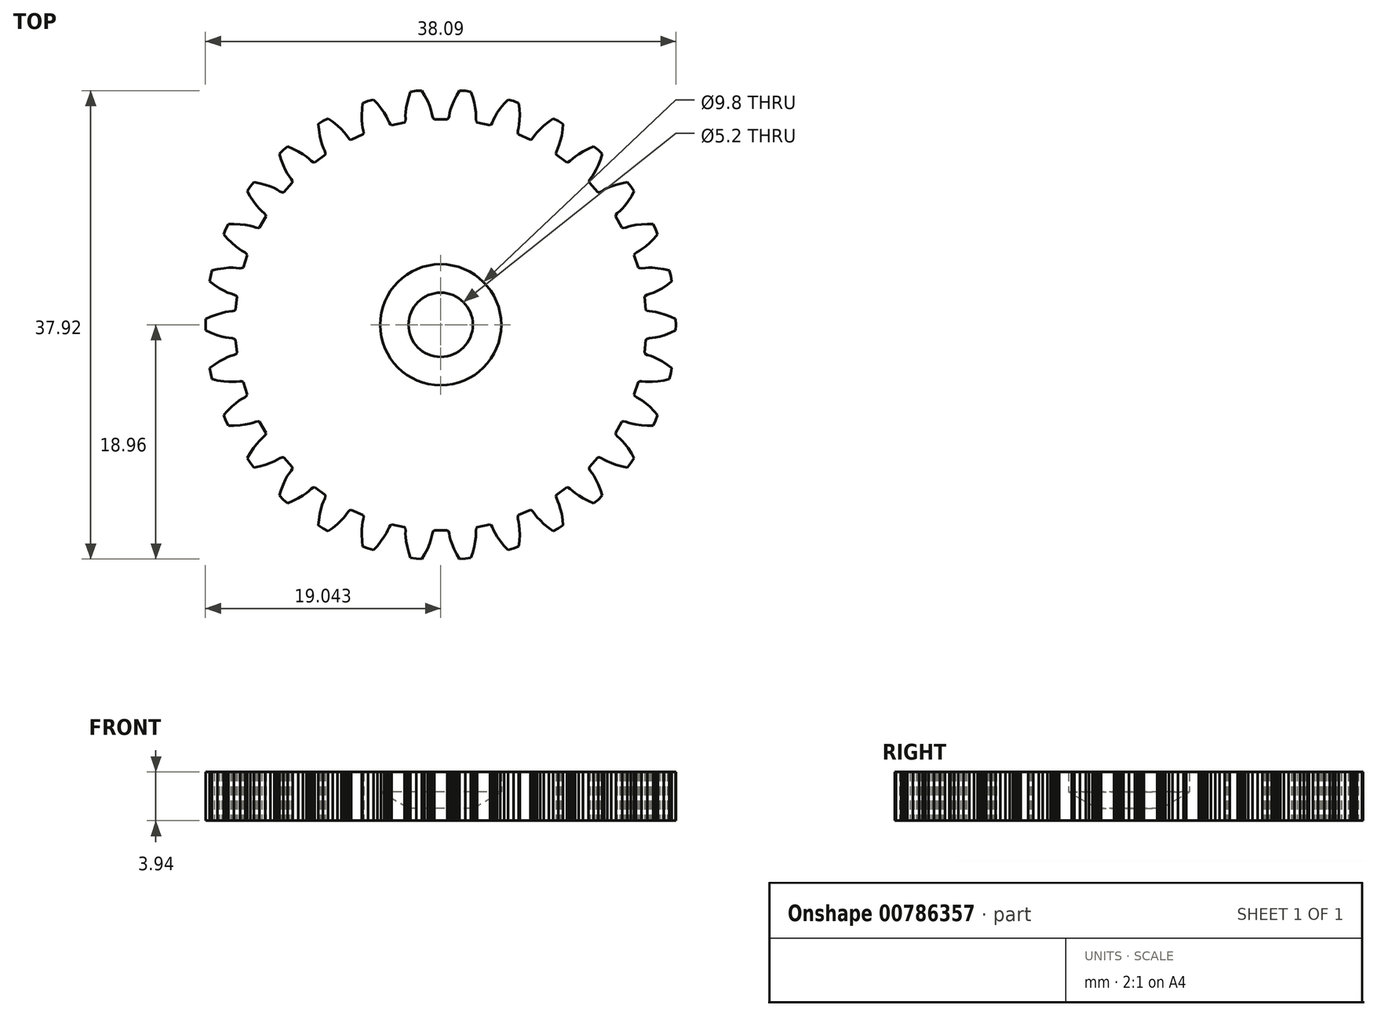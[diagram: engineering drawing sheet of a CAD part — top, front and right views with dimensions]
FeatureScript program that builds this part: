
annotation { "Feature Type Name" : "Feature", "Feature Type Description" : "" }
export const myFeature = defineFeature(function(context is Context, id is Id, definition is map)
    precondition{}
    {
        {
            var Q0;
            Q0=qCreatedBy(makeId("Top.planeOp"),FACE);
            var sketch = newSketch(context, id + "F0", { "sketchPlane" : qUnion([Q0])});
            skLineSegment(sketch, "E0", {"start": v(756.52, -239.33) * mm, "end": v(762.99, -215.17) * mm});
            skLineSegment(sketch, "E1", {"start": v(762.99, -215.17) * mm, "end": v(766.9, -190.46) * mm});
            skLineSegment(sketch, "E2", {"start": v(766.9, -190.46) * mm, "end": v(747.41, -175.84) * mm});
            skLineSegment(sketch, "E3", {"start": v(747.41, -175.84) * mm, "end": v(724.34, -160.92) * mm});
            skLineSegment(sketch, "E4", {"start": v(724.34, -160.92) * mm, "end": v(704.2, -149.81) * mm});
            skLineSegment(sketch, "E5", {"start": v(704.2, -149.81) * mm, "end": v(687.39, -142.02) * mm});
            skLineSegment(sketch, "E6", {"start": v(687.39, -142.02) * mm, "end": v(674.26, -137) * mm});
            skLineSegment(sketch, "E7", {"start": v(674.26, -137) * mm, "end": v(660.16, -132.73) * mm});
            skLineSegment(sketch, "E8", {"start": v(660.16, -132.73) * mm, "end": v(651.05, -128.15) * mm});
            skLineSegment(sketch, "E9", {"start": v(651.05, -128.15) * mm, "end": v(647, -123.28) * mm});
            skLineSegment(sketch, "E10", {"start": v(647, -123.28) * mm, "end": v(653.04, -65.76) * mm});
            skLineSegment(sketch, "E11", {"start": v(653.04, -65.76) * mm, "end": v(658.02, -61.84) * mm});
            skLineSegment(sketch, "E12", {"start": v(658.02, -61.84) * mm, "end": v(667.88, -59.26) * mm});
            skLineSegment(sketch, "E13", {"start": v(667.88, -59.26) * mm, "end": v(682.56, -58) * mm});
            skLineSegment(sketch, "E14", {"start": v(682.56, -58) * mm, "end": v(696.45, -55.83) * mm});
            skLineSegment(sketch, "E15", {"start": v(696.45, -55.83) * mm, "end": v(714.5, -51.7) * mm});
            skLineSegment(sketch, "E16", {"start": v(714.5, -51.7) * mm, "end": v(736.52, -45.02) * mm});
            skLineSegment(sketch, "E17", {"start": v(736.52, -45.02) * mm, "end": v(762.2, -35.23) * mm});
            skLineSegment(sketch, "E18", {"start": v(762.2, -35.23) * mm, "end": v(784.3, -24.98) * mm});
            skLineSegment(sketch, "E19", {"start": v(784.3, -24.98) * mm, "end": v(785.6, 0) * mm});
            skLineSegment(sketch, "E20", {"start": v(785.6, 0) * mm, "end": v(784.3, 24.98) * mm});
            skLineSegment(sketch, "E21", {"start": v(784.3, 24.98) * mm, "end": v(762.2, 35.23) * mm});
            skLineSegment(sketch, "E22", {"start": v(762.2, 35.23) * mm, "end": v(736.52, 45.02) * mm});
            skLineSegment(sketch, "E23", {"start": v(736.52, 45.02) * mm, "end": v(714.5, 51.7) * mm});
            skLineSegment(sketch, "E24", {"start": v(714.5, 51.7) * mm, "end": v(696.45, 55.83) * mm});
            skLineSegment(sketch, "E25", {"start": v(696.45, 55.83) * mm, "end": v(682.56, 58) * mm});
            skLineSegment(sketch, "E26", {"start": v(682.56, 58) * mm, "end": v(667.88, 59.26) * mm});
            skLineSegment(sketch, "E27", {"start": v(667.88, 59.26) * mm, "end": v(658.02, 61.84) * mm});
            skLineSegment(sketch, "E28", {"start": v(658.02, 61.84) * mm, "end": v(653.04, 65.76) * mm});
            skLineSegment(sketch, "E29", {"start": v(653.04, 65.76) * mm, "end": v(647, 123.28) * mm});
            skLineSegment(sketch, "E30", {"start": v(647, 123.28) * mm, "end": v(651.05, 128.15) * mm});
            skLineSegment(sketch, "E31", {"start": v(651.05, 128.15) * mm, "end": v(660.16, 132.73) * mm});
            skLineSegment(sketch, "E32", {"start": v(660.16, 132.73) * mm, "end": v(674.26, 137) * mm});
            skLineSegment(sketch, "E33", {"start": v(674.26, 137) * mm, "end": v(687.39, 142.02) * mm});
            skLineSegment(sketch, "E34", {"start": v(687.39, 142.02) * mm, "end": v(704.2, 149.81) * mm});
            skLineSegment(sketch, "E35", {"start": v(704.2, 149.81) * mm, "end": v(724.34, 160.92) * mm});
            skLineSegment(sketch, "E36", {"start": v(724.34, 160.92) * mm, "end": v(747.41, 175.84) * mm});
            skLineSegment(sketch, "E37", {"start": v(747.41, 175.84) * mm, "end": v(766.9, 190.46) * mm});
            skLineSegment(sketch, "E38", {"start": v(766.9, 190.46) * mm, "end": v(762.99, 215.17) * mm});
            skLineSegment(sketch, "E39", {"start": v(762.99, 215.17) * mm, "end": v(756.52, 239.33) * mm});
            skLineSegment(sketch, "E40", {"start": v(756.52, 239.33) * mm, "end": v(732.77, 244.76) * mm});
            skLineSegment(sketch, "E41", {"start": v(732.77, 244.76) * mm, "end": v(705.62, 249) * mm});
            skLineSegment(sketch, "E42", {"start": v(705.62, 249) * mm, "end": v(682.7, 250.96) * mm});
            skLineSegment(sketch, "E43", {"start": v(682.7, 250.96) * mm, "end": v(664.17, 251.24) * mm});
            skLineSegment(sketch, "E44", {"start": v(664.17, 251.24) * mm, "end": v(650.14, 250.48) * mm});
            skLineSegment(sketch, "E45", {"start": v(650.14, 250.48) * mm, "end": v(635.52, 248.65) * mm});
            skLineSegment(sketch, "E46", {"start": v(635.52, 248.65) * mm, "end": v(625.33, 249.13) * mm});
            skLineSegment(sketch, "E47", {"start": v(625.33, 249.13) * mm, "end": v(619.65, 251.93) * mm});
            skLineSegment(sketch, "E48", {"start": v(619.65, 251.93) * mm, "end": v(601.78, 306.93) * mm});
            skLineSegment(sketch, "E49", {"start": v(601.78, 306.93) * mm, "end": v(604.73, 312.54) * mm});
            skLineSegment(sketch, "E50", {"start": v(604.73, 312.54) * mm, "end": v(612.69, 318.91) * mm});
            skLineSegment(sketch, "E51", {"start": v(612.69, 318.91) * mm, "end": v(625.6, 326.03) * mm});
            skLineSegment(sketch, "E52", {"start": v(625.6, 326.03) * mm, "end": v(637.4, 333.66) * mm});
            skLineSegment(sketch, "E53", {"start": v(637.4, 333.66) * mm, "end": v(652.21, 344.78) * mm});
            skLineSegment(sketch, "E54", {"start": v(652.21, 344.78) * mm, "end": v(669.6, 359.83) * mm});
            skLineSegment(sketch, "E55", {"start": v(669.6, 359.83) * mm, "end": v(689.07, 379.22) * mm});
            skLineSegment(sketch, "E56", {"start": v(689.07, 379.22) * mm, "end": v(705.1, 397.58) * mm});
            skLineSegment(sketch, "E57", {"start": v(705.1, 397.58) * mm, "end": v(696.13, 420.93) * mm});
            skLineSegment(sketch, "E58", {"start": v(696.13, 420.93) * mm, "end": v(684.78, 443.21) * mm});
            skLineSegment(sketch, "E59", {"start": v(684.78, 443.21) * mm, "end": v(660.42, 443.59) * mm});
            skLineSegment(sketch, "E60", {"start": v(660.42, 443.59) * mm, "end": v(632.98, 442.1) * mm});
            skLineSegment(sketch, "E61", {"start": v(632.98, 442.1) * mm, "end": v(610.15, 439.24) * mm});
            skLineSegment(sketch, "E62", {"start": v(610.15, 439.24) * mm, "end": v(591.97, 435.67) * mm});
            skLineSegment(sketch, "E63", {"start": v(591.97, 435.67) * mm, "end": v(578.41, 432) * mm});
            skLineSegment(sketch, "E64", {"start": v(578.41, 432) * mm, "end": v(564.49, 427.18) * mm});
            skLineSegment(sketch, "E65", {"start": v(564.49, 427.18) * mm, "end": v(554.43, 425.53) * mm});
            skLineSegment(sketch, "E66", {"start": v(554.43, 425.53) * mm, "end": v(548.28, 427.08) * mm});
            skLineSegment(sketch, "E67", {"start": v(548.28, 427.08) * mm, "end": v(519.37, 477.17) * mm});
            skLineSegment(sketch, "E68", {"start": v(519.37, 477.17) * mm, "end": v(521.09, 483.27) * mm});
            skLineSegment(sketch, "E69", {"start": v(521.09, 483.27) * mm, "end": v(527.55, 491.16) * mm});
            skLineSegment(sketch, "E70", {"start": v(527.55, 491.16) * mm, "end": v(538.7, 500.8) * mm});
            skLineSegment(sketch, "E71", {"start": v(538.7, 500.8) * mm, "end": v(548.65, 510.72) * mm});
            skLineSegment(sketch, "E72", {"start": v(548.65, 510.72) * mm, "end": v(560.83, 524.67) * mm});
            skLineSegment(sketch, "E73", {"start": v(560.83, 524.67) * mm, "end": v(574.71, 543.02) * mm});
            skLineSegment(sketch, "E74", {"start": v(574.71, 543.02) * mm, "end": v(589.72, 566.03) * mm});
            skLineSegment(sketch, "E75", {"start": v(589.72, 566.03) * mm, "end": v(601.58, 587.32) * mm});
            skLineSegment(sketch, "E76", {"start": v(601.58, 587.32) * mm, "end": v(587.96, 608.3) * mm});
            skLineSegment(sketch, "E77", {"start": v(587.96, 608.3) * mm, "end": v(572.22, 627.73) * mm});
            skLineSegment(sketch, "E78", {"start": v(572.22, 627.73) * mm, "end": v(548.31, 623.03) * mm});
            skLineSegment(sketch, "E79", {"start": v(548.31, 623.03) * mm, "end": v(521.78, 615.87) * mm});
            skLineSegment(sketch, "E80", {"start": v(521.78, 615.87) * mm, "end": v(500.05, 608.33) * mm});
            skLineSegment(sketch, "E81", {"start": v(500.05, 608.33) * mm, "end": v(483.01, 601.06) * mm});
            skLineSegment(sketch, "E82", {"start": v(483.01, 601.06) * mm, "end": v(470.5, 594.65) * mm});
            skLineSegment(sketch, "E83", {"start": v(470.5, 594.65) * mm, "end": v(457.89, 587.04) * mm});
            skLineSegment(sketch, "E84", {"start": v(457.89, 587.04) * mm, "end": v(448.4, 583.33) * mm});
            skLineSegment(sketch, "E85", {"start": v(448.4, 583.33) * mm, "end": v(442.06, 583.58) * mm});
            skLineSegment(sketch, "E86", {"start": v(442.06, 583.58) * mm, "end": v(403.36, 626.56) * mm});
            skLineSegment(sketch, "E87", {"start": v(403.36, 626.56) * mm, "end": v(403.77, 632.88) * mm});
            skLineSegment(sketch, "E88", {"start": v(403.77, 632.88) * mm, "end": v(408.45, 641.94) * mm});
            skLineSegment(sketch, "E89", {"start": v(408.45, 641.94) * mm, "end": v(417.35, 653.69) * mm});
            skLineSegment(sketch, "E90", {"start": v(417.35, 653.69) * mm, "end": v(425.03, 665.46) * mm});
            skLineSegment(sketch, "E91", {"start": v(425.03, 665.46) * mm, "end": v(434.04, 681.64) * mm});
            skLineSegment(sketch, "E92", {"start": v(434.04, 681.64) * mm, "end": v(443.8, 702.47) * mm});
            skLineSegment(sketch, "E93", {"start": v(443.8, 702.47) * mm, "end": v(453.7, 728.1) * mm});
            skLineSegment(sketch, "E94", {"start": v(453.7, 728.1) * mm, "end": v(460.88, 751.39) * mm});
            skLineSegment(sketch, "E95", {"start": v(460.88, 751.39) * mm, "end": v(443.2, 769.07) * mm});
            skLineSegment(sketch, "E96", {"start": v(443.2, 769.07) * mm, "end": v(423.75, 784.81) * mm});
            skLineSegment(sketch, "E97", {"start": v(423.75, 784.81) * mm, "end": v(401.35, 775.25) * mm});
            skLineSegment(sketch, "E98", {"start": v(401.35, 775.25) * mm, "end": v(376.89, 762.72) * mm});
            skLineSegment(sketch, "E99", {"start": v(376.89, 762.72) * mm, "end": v(357.2, 750.83) * mm});
            skLineSegment(sketch, "E100", {"start": v(357.2, 750.83) * mm, "end": v(342.04, 740.18) * mm});
            skLineSegment(sketch, "E101", {"start": v(342.04, 740.18) * mm, "end": v(331.14, 731.31) * mm});
            skLineSegment(sketch, "E102", {"start": v(331.14, 731.31) * mm, "end": v(320.38, 721.24) * mm});
            skLineSegment(sketch, "E103", {"start": v(320.38, 721.24) * mm, "end": v(311.86, 715.64) * mm});
            skLineSegment(sketch, "E104", {"start": v(311.86, 715.64) * mm, "end": v(305.62, 714.56) * mm});
            skLineSegment(sketch, "E105", {"start": v(305.62, 714.56) * mm, "end": v(258.83, 748.56) * mm});
            skLineSegment(sketch, "E106", {"start": v(258.83, 748.56) * mm, "end": v(257.92, 754.83) * mm});
            skLineSegment(sketch, "E107", {"start": v(257.92, 754.83) * mm, "end": v(260.62, 764.66) * mm});
            skLineSegment(sketch, "E108", {"start": v(260.62, 764.66) * mm, "end": v(266.87, 778) * mm});
            skLineSegment(sketch, "E109", {"start": v(266.87, 778) * mm, "end": v(271.93, 791.11) * mm});
            skLineSegment(sketch, "E110", {"start": v(271.93, 791.11) * mm, "end": v(277.39, 808.82) * mm});
            skLineSegment(sketch, "E111", {"start": v(277.39, 808.82) * mm, "end": v(282.6, 831.22) * mm});
            skLineSegment(sketch, "E112", {"start": v(282.6, 831.22) * mm, "end": v(286.96, 858.35) * mm});
            skLineSegment(sketch, "E113", {"start": v(286.96, 858.35) * mm, "end": v(289.14, 882.62) * mm});
            skLineSegment(sketch, "E114", {"start": v(289.14, 882.62) * mm, "end": v(268.16, 896.24) * mm});
            skLineSegment(sketch, "E115", {"start": v(268.16, 896.24) * mm, "end": v(245.87, 907.6) * mm});
            skLineSegment(sketch, "E116", {"start": v(245.87, 907.6) * mm, "end": v(225.94, 893.58) * mm});
            skLineSegment(sketch, "E117", {"start": v(225.94, 893.58) * mm, "end": v(204.63, 876.24) * mm});
            skLineSegment(sketch, "E118", {"start": v(204.63, 876.24) * mm, "end": v(187.83, 860.52) * mm});
            skLineSegment(sketch, "E119", {"start": v(187.83, 860.52) * mm, "end": v(175.23, 846.94) * mm});
            skLineSegment(sketch, "E120", {"start": v(175.23, 846.94) * mm, "end": v(166.4, 836) * mm});
            skLineSegment(sketch, "E121", {"start": v(166.4, 836) * mm, "end": v(157.98, 823.92) * mm});
            skLineSegment(sketch, "E122", {"start": v(157.98, 823.92) * mm, "end": v(150.81, 816.67) * mm});
            skLineSegment(sketch, "E123", {"start": v(150.81, 816.67) * mm, "end": v(144.93, 814.32) * mm});
            skLineSegment(sketch, "E124", {"start": v(144.93, 814.32) * mm, "end": v(92.1, 837.84) * mm});
            skLineSegment(sketch, "E125", {"start": v(92.1, 837.84) * mm, "end": v(89.9, 843.79) * mm});
            skLineSegment(sketch, "E126", {"start": v(89.9, 843.79) * mm, "end": v(90.5, 853.97) * mm});
            skLineSegment(sketch, "E127", {"start": v(90.5, 853.97) * mm, "end": v(93.84, 868.32) * mm});
            skLineSegment(sketch, "E128", {"start": v(93.84, 868.32) * mm, "end": v(96.06, 882.2) * mm});
            skLineSegment(sketch, "E129", {"start": v(96.06, 882.2) * mm, "end": v(97.72, 900.64) * mm});
            skLineSegment(sketch, "E130", {"start": v(97.72, 900.64) * mm, "end": v(98.16, 923.64) * mm});
            skLineSegment(sketch, "E131", {"start": v(98.16, 923.64) * mm, "end": v(96.78, 951.09) * mm});
            skLineSegment(sketch, "E132", {"start": v(96.78, 951.09) * mm, "end": v(93.86, 975.27) * mm});
            skLineSegment(sketch, "E133", {"start": v(93.86, 975.27) * mm, "end": v(70.51, 984.24) * mm});
            skLineSegment(sketch, "E134", {"start": v(70.51, 984.24) * mm, "end": v(46.35, 990.71) * mm});
            skLineSegment(sketch, "E135", {"start": v(46.35, 990.71) * mm, "end": v(29.77, 972.86) * mm});
            skLineSegment(sketch, "E136", {"start": v(29.77, 972.86) * mm, "end": v(12.53, 951.47) * mm});
            skLineSegment(sketch, "E137", {"start": v(12.53, 951.47) * mm, "end": v(-0.63, 932.6) * mm});
            skLineSegment(sketch, "E138", {"start": v(-0.63, 932.6) * mm, "end": v(-10.14, 916.7) * mm});
            skLineSegment(sketch, "E139", {"start": v(-10.14, 916.7) * mm, "end": v(-16.5, 904.17) * mm});
            skLineSegment(sketch, "E140", {"start": v(-16.5, 904.17) * mm, "end": v(-22.22, 890.59) * mm});
            skLineSegment(sketch, "E141", {"start": v(-22.22, 890.59) * mm, "end": v(-27.73, 882) * mm});
            skLineSegment(sketch, "E142", {"start": v(-27.73, 882) * mm, "end": v(-33, 878.49) * mm});
            skLineSegment(sketch, "E143", {"start": v(-33, 878.49) * mm, "end": v(-89.57, 890.51) * mm});
            skLineSegment(sketch, "E144", {"start": v(-89.57, 890.51) * mm, "end": v(-92.95, 895.87) * mm});
            skLineSegment(sketch, "E145", {"start": v(-92.95, 895.87) * mm, "end": v(-94.48, 905.95) * mm});
            skLineSegment(sketch, "E146", {"start": v(-94.48, 905.95) * mm, "end": v(-94.2, 920.68) * mm});
            skLineSegment(sketch, "E147", {"start": v(-94.2, 920.68) * mm, "end": v(-94.9, 934.72) * mm});
            skLineSegment(sketch, "E148", {"start": v(-94.9, 934.72) * mm, "end": v(-97.12, 953.1) * mm});
            skLineSegment(sketch, "E149", {"start": v(-97.12, 953.1) * mm, "end": v(-101.46, 975.7) * mm});
            skLineSegment(sketch, "E150", {"start": v(-101.46, 975.7) * mm, "end": v(-108.52, 1002.25) * mm});
            skLineSegment(sketch, "E151", {"start": v(-108.52, 1002.25) * mm, "end": v(-116.4, 1025.3) * mm});
            skLineSegment(sketch, "E152", {"start": v(-116.4, 1025.3) * mm, "end": v(-141.11, 1029.22) * mm});
            skLineSegment(sketch, "E153", {"start": v(-141.11, 1029.22) * mm, "end": v(-166.09, 1030.53) * mm});
            skLineSegment(sketch, "E154", {"start": v(-166.09, 1030.53) * mm, "end": v(-178.6, 1009.62) * mm});
            skLineSegment(sketch, "E155", {"start": v(-178.6, 1009.62) * mm, "end": v(-191.02, 985.11) * mm});
            skLineSegment(sketch, "E156", {"start": v(-191.02, 985.11) * mm, "end": v(-199.96, 963.92) * mm});
            skLineSegment(sketch, "E157", {"start": v(-199.96, 963.92) * mm, "end": v(-205.96, 946.39) * mm});
            skLineSegment(sketch, "E158", {"start": v(-205.96, 946.39) * mm, "end": v(-209.57, 932.8) * mm});
            skLineSegment(sketch, "E159", {"start": v(-209.57, 932.8) * mm, "end": v(-212.35, 918.34) * mm});
            skLineSegment(sketch, "E160", {"start": v(-212.35, 918.34) * mm, "end": v(-215.95, 908.8) * mm});
            skLineSegment(sketch, "E161", {"start": v(-215.95, 908.8) * mm, "end": v(-220.37, 904.26) * mm});
            skLineSegment(sketch, "E162", {"start": v(-220.37, 904.26) * mm, "end": v(-278.2, 904.26) * mm});
            skLineSegment(sketch, "E163", {"start": v(-278.2, 904.26) * mm, "end": v(-282.62, 908.8) * mm});
            skLineSegment(sketch, "E164", {"start": v(-282.62, 908.8) * mm, "end": v(-286.22, 918.34) * mm});
            skLineSegment(sketch, "E165", {"start": v(-286.22, 918.34) * mm, "end": v(-289, 932.8) * mm});
            skLineSegment(sketch, "E166", {"start": v(-289, 932.8) * mm, "end": v(-292.61, 946.39) * mm});
            skLineSegment(sketch, "E167", {"start": v(-292.61, 946.39) * mm, "end": v(-298.6, 963.92) * mm});
            skLineSegment(sketch, "E168", {"start": v(-298.6, 963.92) * mm, "end": v(-307.55, 985.11) * mm});
            skLineSegment(sketch, "E169", {"start": v(-307.55, 985.11) * mm, "end": v(-319.98, 1009.62) * mm});
            skLineSegment(sketch, "E170", {"start": v(-319.98, 1009.62) * mm, "end": v(-332.48, 1030.53) * mm});
            skLineSegment(sketch, "E171", {"start": v(-332.48, 1030.53) * mm, "end": v(-357.46, 1029.22) * mm});
            skLineSegment(sketch, "E172", {"start": v(-357.46, 1029.22) * mm, "end": v(-382.16, 1025.3) * mm});
            skLineSegment(sketch, "E173", {"start": v(-382.16, 1025.3) * mm, "end": v(-390.05, 1002.25) * mm});
            skLineSegment(sketch, "E174", {"start": v(-390.05, 1002.25) * mm, "end": v(-397.1, 975.7) * mm});
            skLineSegment(sketch, "E175", {"start": v(-397.1, 975.7) * mm, "end": v(-401.45, 953.1) * mm});
            skLineSegment(sketch, "E176", {"start": v(-401.45, 953.1) * mm, "end": v(-403.67, 934.72) * mm});
            skLineSegment(sketch, "E177", {"start": v(-403.67, 934.72) * mm, "end": v(-404.38, 920.68) * mm});
            skLineSegment(sketch, "E178", {"start": v(-404.38, 920.68) * mm, "end": v(-404.09, 905.95) * mm});
            skLineSegment(sketch, "E179", {"start": v(-404.09, 905.95) * mm, "end": v(-405.62, 895.87) * mm});
            skLineSegment(sketch, "E180", {"start": v(-405.62, 895.87) * mm, "end": v(-409, 890.51) * mm});
            skLineSegment(sketch, "E181", {"start": v(-409, 890.51) * mm, "end": v(-465.58, 878.49) * mm});
            skLineSegment(sketch, "E182", {"start": v(-465.58, 878.49) * mm, "end": v(-470.85, 882) * mm});
            skLineSegment(sketch, "E183", {"start": v(-470.85, 882) * mm, "end": v(-476.35, 890.59) * mm});
            skLineSegment(sketch, "E184", {"start": v(-476.35, 890.59) * mm, "end": v(-482.08, 904.17) * mm});
            skLineSegment(sketch, "E185", {"start": v(-482.08, 904.17) * mm, "end": v(-488.43, 916.7) * mm});
            skLineSegment(sketch, "E186", {"start": v(-488.43, 916.7) * mm, "end": v(-497.94, 932.6) * mm});
            skLineSegment(sketch, "E187", {"start": v(-497.94, 932.6) * mm, "end": v(-511.1, 951.47) * mm});
            skLineSegment(sketch, "E188", {"start": v(-511.1, 951.47) * mm, "end": v(-528.35, 972.86) * mm});
            skLineSegment(sketch, "E189", {"start": v(-528.35, 972.86) * mm, "end": v(-544.92, 990.71) * mm});
            skLineSegment(sketch, "E190", {"start": v(-544.92, 990.71) * mm, "end": v(-569.08, 984.24) * mm});
            skLineSegment(sketch, "E191", {"start": v(-569.08, 984.24) * mm, "end": v(-592.43, 975.27) * mm});
            skLineSegment(sketch, "E192", {"start": v(-592.43, 975.27) * mm, "end": v(-595.35, 951.09) * mm});
            skLineSegment(sketch, "E193", {"start": v(-595.35, 951.09) * mm, "end": v(-596.74, 923.64) * mm});
            skLineSegment(sketch, "E194", {"start": v(-596.74, 923.64) * mm, "end": v(-596.29, 900.64) * mm});
            skLineSegment(sketch, "E195", {"start": v(-596.29, 900.64) * mm, "end": v(-594.63, 882.2) * mm});
            skLineSegment(sketch, "E196", {"start": v(-594.63, 882.2) * mm, "end": v(-592.4, 868.32) * mm});
            skLineSegment(sketch, "E197", {"start": v(-592.4, 868.32) * mm, "end": v(-589.06, 853.97) * mm});
            skLineSegment(sketch, "E198", {"start": v(-589.06, 853.97) * mm, "end": v(-588.47, 843.79) * mm});
            skLineSegment(sketch, "E199", {"start": v(-588.47, 843.79) * mm, "end": v(-590.66, 837.84) * mm});
            skLineSegment(sketch, "E200", {"start": v(-590.66, 837.84) * mm, "end": v(-643.5, 814.32) * mm});
            skLineSegment(sketch, "E201", {"start": v(-643.5, 814.32) * mm, "end": v(-649.38, 816.67) * mm});
            skLineSegment(sketch, "E202", {"start": v(-649.38, 816.67) * mm, "end": v(-656.55, 823.92) * mm});
            skLineSegment(sketch, "E203", {"start": v(-656.55, 823.92) * mm, "end": v(-664.98, 836) * mm});
            skLineSegment(sketch, "E204", {"start": v(-664.98, 836) * mm, "end": v(-673.8, 846.94) * mm});
            skLineSegment(sketch, "E205", {"start": v(-673.8, 846.94) * mm, "end": v(-686.4, 860.52) * mm});
            skLineSegment(sketch, "E206", {"start": v(-686.4, 860.52) * mm, "end": v(-703.2, 876.24) * mm});
            skLineSegment(sketch, "E207", {"start": v(-703.2, 876.24) * mm, "end": v(-724.52, 893.58) * mm});
            skLineSegment(sketch, "E208", {"start": v(-724.52, 893.58) * mm, "end": v(-744.44, 907.6) * mm});
            skLineSegment(sketch, "E209", {"start": v(-744.44, 907.6) * mm, "end": v(-766.73, 896.24) * mm});
            skLineSegment(sketch, "E210", {"start": v(-766.73, 896.24) * mm, "end": v(-787.7, 882.62) * mm});
            skLineSegment(sketch, "E211", {"start": v(-787.7, 882.62) * mm, "end": v(-785.53, 858.35) * mm});
            skLineSegment(sketch, "E212", {"start": v(-785.53, 858.35) * mm, "end": v(-781.18, 831.22) * mm});
            skLineSegment(sketch, "E213", {"start": v(-781.18, 831.22) * mm, "end": v(-775.96, 808.82) * mm});
            skLineSegment(sketch, "E214", {"start": v(-775.96, 808.82) * mm, "end": v(-770.5, 791.11) * mm});
            skLineSegment(sketch, "E215", {"start": v(-770.5, 791.11) * mm, "end": v(-765.44, 778) * mm});
            skLineSegment(sketch, "E216", {"start": v(-765.44, 778) * mm, "end": v(-759.19, 764.66) * mm});
            skLineSegment(sketch, "E217", {"start": v(-759.19, 764.66) * mm, "end": v(-756.5, 754.83) * mm});
            skLineSegment(sketch, "E218", {"start": v(-756.5, 754.83) * mm, "end": v(-757.4, 748.56) * mm});
            skLineSegment(sketch, "E219", {"start": v(-757.4, 748.56) * mm, "end": v(-804.2, 714.56) * mm});
            skLineSegment(sketch, "E220", {"start": v(-804.2, 714.56) * mm, "end": v(-810.44, 715.64) * mm});
            skLineSegment(sketch, "E221", {"start": v(-810.44, 715.64) * mm, "end": v(-818.95, 721.24) * mm});
            skLineSegment(sketch, "E222", {"start": v(-818.95, 721.24) * mm, "end": v(-829.71, 731.31) * mm});
            skLineSegment(sketch, "E223", {"start": v(-829.71, 731.31) * mm, "end": v(-840.61, 740.18) * mm});
            skLineSegment(sketch, "E224", {"start": v(-840.61, 740.18) * mm, "end": v(-855.77, 750.83) * mm});
            skLineSegment(sketch, "E225", {"start": v(-855.77, 750.83) * mm, "end": v(-875.46, 762.72) * mm});
            skLineSegment(sketch, "E226", {"start": v(-875.46, 762.72) * mm, "end": v(-899.92, 775.25) * mm});
            skLineSegment(sketch, "E227", {"start": v(-899.92, 775.25) * mm, "end": v(-922.32, 784.81) * mm});
            skLineSegment(sketch, "E228", {"start": v(-922.32, 784.81) * mm, "end": v(-941.76, 769.07) * mm});
            skLineSegment(sketch, "E229", {"start": v(-941.76, 769.07) * mm, "end": v(-959.45, 751.39) * mm});
            skLineSegment(sketch, "E230", {"start": v(-959.45, 751.39) * mm, "end": v(-952.28, 728.1) * mm});
            skLineSegment(sketch, "E231", {"start": v(-952.28, 728.1) * mm, "end": v(-942.38, 702.47) * mm});
            skLineSegment(sketch, "E232", {"start": v(-942.38, 702.47) * mm, "end": v(-932.61, 681.64) * mm});
            skLineSegment(sketch, "E233", {"start": v(-932.61, 681.64) * mm, "end": v(-923.6, 665.46) * mm});
            skLineSegment(sketch, "E234", {"start": v(-923.6, 665.46) * mm, "end": v(-915.92, 653.69) * mm});
            skLineSegment(sketch, "E235", {"start": v(-915.92, 653.69) * mm, "end": v(-907.03, 641.94) * mm});
            skLineSegment(sketch, "E236", {"start": v(-907.03, 641.94) * mm, "end": v(-902.35, 632.88) * mm});
            skLineSegment(sketch, "E237", {"start": v(-902.35, 632.88) * mm, "end": v(-901.93, 626.56) * mm});
            skLineSegment(sketch, "E238", {"start": v(-901.93, 626.56) * mm, "end": v(-940.63, 583.58) * mm});
            skLineSegment(sketch, "E239", {"start": v(-940.63, 583.58) * mm, "end": v(-946.96, 583.33) * mm});
            skLineSegment(sketch, "E240", {"start": v(-946.96, 583.33) * mm, "end": v(-956.46, 587.04) * mm});
            skLineSegment(sketch, "E241", {"start": v(-956.46, 587.04) * mm, "end": v(-969.07, 594.65) * mm});
            skLineSegment(sketch, "E242", {"start": v(-969.07, 594.65) * mm, "end": v(-981.58, 601.06) * mm});
            skLineSegment(sketch, "E243", {"start": v(-981.58, 601.06) * mm, "end": v(-998.62, 608.33) * mm});
            skLineSegment(sketch, "E244", {"start": v(-998.62, 608.33) * mm, "end": v(-1020.35, 615.87) * mm});
            skLineSegment(sketch, "E245", {"start": v(-1020.35, 615.87) * mm, "end": v(-1046.88, 623.03) * mm});
            skLineSegment(sketch, "E246", {"start": v(-1046.88, 623.03) * mm, "end": v(-1070.79, 627.73) * mm});
            skLineSegment(sketch, "E247", {"start": v(-1070.79, 627.73) * mm, "end": v(-1086.53, 608.3) * mm});
            skLineSegment(sketch, "E248", {"start": v(-1086.53, 608.3) * mm, "end": v(-1100.15, 587.32) * mm});
            skLineSegment(sketch, "E249", {"start": v(-1100.15, 587.32) * mm, "end": v(-1088.3, 566.03) * mm});
            skLineSegment(sketch, "E250", {"start": v(-1088.3, 566.03) * mm, "end": v(-1073.28, 543.02) * mm});
            skLineSegment(sketch, "E251", {"start": v(-1073.28, 543.02) * mm, "end": v(-1059.4, 524.67) * mm});
            skLineSegment(sketch, "E252", {"start": v(-1059.4, 524.67) * mm, "end": v(-1047.22, 510.72) * mm});
            skLineSegment(sketch, "E253", {"start": v(-1047.22, 510.72) * mm, "end": v(-1037.26, 500.8) * mm});
            skLineSegment(sketch, "E254", {"start": v(-1037.26, 500.8) * mm, "end": v(-1026.12, 491.16) * mm});
            skLineSegment(sketch, "E255", {"start": v(-1026.12, 491.16) * mm, "end": v(-1019.66, 483.27) * mm});
            skLineSegment(sketch, "E256", {"start": v(-1019.66, 483.27) * mm, "end": v(-1017.94, 477.17) * mm});
            skLineSegment(sketch, "E257", {"start": v(-1017.94, 477.17) * mm, "end": v(-1046.86, 427.08) * mm});
            skLineSegment(sketch, "E258", {"start": v(-1046.86, 427.08) * mm, "end": v(-1053, 425.53) * mm});
            skLineSegment(sketch, "E259", {"start": v(-1053, 425.53) * mm, "end": v(-1063.06, 427.18) * mm});
            skLineSegment(sketch, "E260", {"start": v(-1063.06, 427.18) * mm, "end": v(-1076.98, 432) * mm});
            skLineSegment(sketch, "E261", {"start": v(-1076.98, 432) * mm, "end": v(-1090.55, 435.67) * mm});
            skLineSegment(sketch, "E262", {"start": v(-1090.55, 435.67) * mm, "end": v(-1108.72, 439.24) * mm});
            skLineSegment(sketch, "E263", {"start": v(-1108.72, 439.24) * mm, "end": v(-1131.55, 442.1) * mm});
            skLineSegment(sketch, "E264", {"start": v(-1131.55, 442.1) * mm, "end": v(-1158.99, 443.59) * mm});
            skLineSegment(sketch, "E265", {"start": v(-1158.99, 443.59) * mm, "end": v(-1183.35, 443.21) * mm});
            skLineSegment(sketch, "E266", {"start": v(-1183.35, 443.21) * mm, "end": v(-1194.7, 420.93) * mm});
            skLineSegment(sketch, "E267", {"start": v(-1194.7, 420.93) * mm, "end": v(-1203.67, 397.58) * mm});
            skLineSegment(sketch, "E268", {"start": v(-1203.67, 397.58) * mm, "end": v(-1187.65, 379.22) * mm});
            skLineSegment(sketch, "E269", {"start": v(-1187.65, 379.22) * mm, "end": v(-1168.18, 359.83) * mm});
            skLineSegment(sketch, "E270", {"start": v(-1168.18, 359.83) * mm, "end": v(-1150.78, 344.78) * mm});
            skLineSegment(sketch, "E271", {"start": v(-1150.78, 344.78) * mm, "end": v(-1135.96, 333.66) * mm});
            skLineSegment(sketch, "E272", {"start": v(-1135.96, 333.66) * mm, "end": v(-1124.16, 326.03) * mm});
            skLineSegment(sketch, "E273", {"start": v(-1124.16, 326.03) * mm, "end": v(-1111.26, 318.91) * mm});
            skLineSegment(sketch, "E274", {"start": v(-1111.26, 318.91) * mm, "end": v(-1103.3, 312.54) * mm});
            skLineSegment(sketch, "E275", {"start": v(-1103.3, 312.54) * mm, "end": v(-1100.35, 306.93) * mm});
            skLineSegment(sketch, "E276", {"start": v(-1100.35, 306.93) * mm, "end": v(-1118.22, 251.93) * mm});
            skLineSegment(sketch, "E277", {"start": v(-1118.22, 251.93) * mm, "end": v(-1123.9, 249.13) * mm});
            skLineSegment(sketch, "E278", {"start": v(-1123.9, 249.13) * mm, "end": v(-1134.09, 248.65) * mm});
            skLineSegment(sketch, "E279", {"start": v(-1134.09, 248.65) * mm, "end": v(-1148.71, 250.48) * mm});
            skLineSegment(sketch, "E280", {"start": v(-1148.71, 250.48) * mm, "end": v(-1162.74, 251.24) * mm});
            skLineSegment(sketch, "E281", {"start": v(-1162.74, 251.24) * mm, "end": v(-1181.27, 250.96) * mm});
            skLineSegment(sketch, "E282", {"start": v(-1181.27, 250.96) * mm, "end": v(-1204.19, 249) * mm});
            skLineSegment(sketch, "E283", {"start": v(-1204.19, 249) * mm, "end": v(-1231.34, 244.76) * mm});
            skLineSegment(sketch, "E284", {"start": v(-1231.34, 244.76) * mm, "end": v(-1255.09, 239.33) * mm});
            skLineSegment(sketch, "E285", {"start": v(-1255.09, 239.33) * mm, "end": v(-1261.56, 215.17) * mm});
            skLineSegment(sketch, "E286", {"start": v(-1261.56, 215.17) * mm, "end": v(-1265.47, 190.46) * mm});
            skLineSegment(sketch, "E287", {"start": v(-1265.47, 190.46) * mm, "end": v(-1245.99, 175.84) * mm});
            skLineSegment(sketch, "E288", {"start": v(-1245.99, 175.84) * mm, "end": v(-1222.9, 160.92) * mm});
            skLineSegment(sketch, "E289", {"start": v(-1222.9, 160.92) * mm, "end": v(-1202.77, 149.81) * mm});
            skLineSegment(sketch, "E290", {"start": v(-1202.77, 149.81) * mm, "end": v(-1185.96, 142.02) * mm});
            skLineSegment(sketch, "E291", {"start": v(-1185.96, 142.02) * mm, "end": v(-1172.83, 137) * mm});
            skLineSegment(sketch, "E292", {"start": v(-1172.83, 137) * mm, "end": v(-1158.73, 132.73) * mm});
            skLineSegment(sketch, "E293", {"start": v(-1158.73, 132.73) * mm, "end": v(-1149.62, 128.15) * mm});
            skLineSegment(sketch, "E294", {"start": v(-1149.62, 128.15) * mm, "end": v(-1145.57, 123.28) * mm});
            skLineSegment(sketch, "E295", {"start": v(-1145.57, 123.28) * mm, "end": v(-1151.61, 65.76) * mm});
            skLineSegment(sketch, "E296", {"start": v(-1151.61, 65.76) * mm, "end": v(-1156.59, 61.84) * mm});
            skLineSegment(sketch, "E297", {"start": v(-1156.59, 61.84) * mm, "end": v(-1166.45, 59.26) * mm});
            skLineSegment(sketch, "E298", {"start": v(-1166.45, 59.26) * mm, "end": v(-1181.14, 58) * mm});
            skLineSegment(sketch, "E299", {"start": v(-1181.14, 58) * mm, "end": v(-1195.02, 55.83) * mm});
            skLineSegment(sketch, "E300", {"start": v(-1195.02, 55.83) * mm, "end": v(-1213.08, 51.7) * mm});
            skLineSegment(sketch, "E301", {"start": v(-1213.08, 51.7) * mm, "end": v(-1235.09, 45.02) * mm});
            skLineSegment(sketch, "E302", {"start": v(-1235.09, 45.02) * mm, "end": v(-1260.76, 35.23) * mm});
            skLineSegment(sketch, "E303", {"start": v(-1260.76, 35.23) * mm, "end": v(-1282.87, 24.98) * mm});
            skLineSegment(sketch, "E304", {"start": v(-1282.87, 24.98) * mm, "end": v(-1284.17, 0) * mm});
            skLineSegment(sketch, "E305", {"start": v(-1284.17, 0) * mm, "end": v(-1282.87, -24.98) * mm});
            skLineSegment(sketch, "E306", {"start": v(-1282.87, -24.98) * mm, "end": v(-1260.76, -35.23) * mm});
            skLineSegment(sketch, "E307", {"start": v(-1260.76, -35.23) * mm, "end": v(-1235.09, -45.02) * mm});
            skLineSegment(sketch, "E308", {"start": v(-1235.09, -45.02) * mm, "end": v(-1213.08, -51.7) * mm});
            skLineSegment(sketch, "E309", {"start": v(-1213.08, -51.7) * mm, "end": v(-1195.02, -55.83) * mm});
            skLineSegment(sketch, "E310", {"start": v(-1195.02, -55.83) * mm, "end": v(-1181.14, -58) * mm});
            skLineSegment(sketch, "E311", {"start": v(-1181.14, -58) * mm, "end": v(-1166.45, -59.26) * mm});
            skLineSegment(sketch, "E312", {"start": v(-1166.45, -59.26) * mm, "end": v(-1156.59, -61.84) * mm});
            skLineSegment(sketch, "E313", {"start": v(-1156.59, -61.84) * mm, "end": v(-1151.61, -65.76) * mm});
            skLineSegment(sketch, "E314", {"start": v(-1151.61, -65.76) * mm, "end": v(-1145.57, -123.28) * mm});
            skLineSegment(sketch, "E315", {"start": v(-1145.57, -123.28) * mm, "end": v(-1149.62, -128.15) * mm});
            skLineSegment(sketch, "E316", {"start": v(-1149.62, -128.15) * mm, "end": v(-1158.73, -132.73) * mm});
            skLineSegment(sketch, "E317", {"start": v(-1158.73, -132.73) * mm, "end": v(-1172.83, -137) * mm});
            skLineSegment(sketch, "E318", {"start": v(-1172.83, -137) * mm, "end": v(-1185.96, -142.02) * mm});
            skLineSegment(sketch, "E319", {"start": v(-1185.96, -142.02) * mm, "end": v(-1202.77, -149.81) * mm});
            skLineSegment(sketch, "E320", {"start": v(-1202.77, -149.81) * mm, "end": v(-1222.9, -160.92) * mm});
            skLineSegment(sketch, "E321", {"start": v(-1222.9, -160.92) * mm, "end": v(-1245.99, -175.84) * mm});
            skLineSegment(sketch, "E322", {"start": v(-1245.99, -175.84) * mm, "end": v(-1265.47, -190.46) * mm});
            skLineSegment(sketch, "E323", {"start": v(-1265.47, -190.46) * mm, "end": v(-1261.56, -215.17) * mm});
            skLineSegment(sketch, "E324", {"start": v(-1261.56, -215.17) * mm, "end": v(-1255.09, -239.33) * mm});
            skLineSegment(sketch, "E325", {"start": v(-1255.09, -239.33) * mm, "end": v(-1231.34, -244.76) * mm});
            skLineSegment(sketch, "E326", {"start": v(-1231.34, -244.76) * mm, "end": v(-1204.19, -249) * mm});
            skLineSegment(sketch, "E327", {"start": v(-1204.19, -249) * mm, "end": v(-1181.27, -250.96) * mm});
            skLineSegment(sketch, "E328", {"start": v(-1181.27, -250.96) * mm, "end": v(-1162.74, -251.24) * mm});
            skLineSegment(sketch, "E329", {"start": v(-1162.74, -251.24) * mm, "end": v(-1148.71, -250.48) * mm});
            skLineSegment(sketch, "E330", {"start": v(-1148.71, -250.48) * mm, "end": v(-1134.09, -248.65) * mm});
            skLineSegment(sketch, "E331", {"start": v(-1134.09, -248.65) * mm, "end": v(-1123.9, -249.13) * mm});
            skLineSegment(sketch, "E332", {"start": v(-1123.9, -249.13) * mm, "end": v(-1118.22, -251.93) * mm});
            skLineSegment(sketch, "E333", {"start": v(-1118.22, -251.93) * mm, "end": v(-1100.35, -306.93) * mm});
            skLineSegment(sketch, "E334", {"start": v(-1100.35, -306.93) * mm, "end": v(-1103.3, -312.54) * mm});
            skLineSegment(sketch, "E335", {"start": v(-1103.3, -312.54) * mm, "end": v(-1111.26, -318.91) * mm});
            skLineSegment(sketch, "E336", {"start": v(-1111.26, -318.91) * mm, "end": v(-1124.16, -326.03) * mm});
            skLineSegment(sketch, "E337", {"start": v(-1124.16, -326.03) * mm, "end": v(-1135.96, -333.66) * mm});
            skLineSegment(sketch, "E338", {"start": v(-1135.96, -333.66) * mm, "end": v(-1150.78, -344.78) * mm});
            skLineSegment(sketch, "E339", {"start": v(-1150.78, -344.78) * mm, "end": v(-1168.18, -359.83) * mm});
            skLineSegment(sketch, "E340", {"start": v(-1168.18, -359.83) * mm, "end": v(-1187.65, -379.22) * mm});
            skLineSegment(sketch, "E341", {"start": v(-1187.65, -379.22) * mm, "end": v(-1203.67, -397.58) * mm});
            skLineSegment(sketch, "E342", {"start": v(-1203.67, -397.58) * mm, "end": v(-1194.7, -420.93) * mm});
            skLineSegment(sketch, "E343", {"start": v(-1194.7, -420.93) * mm, "end": v(-1183.35, -443.21) * mm});
            skLineSegment(sketch, "E344", {"start": v(-1183.35, -443.21) * mm, "end": v(-1158.99, -443.59) * mm});
            skLineSegment(sketch, "E345", {"start": v(-1158.99, -443.59) * mm, "end": v(-1131.55, -442.1) * mm});
            skLineSegment(sketch, "E346", {"start": v(-1131.55, -442.1) * mm, "end": v(-1108.72, -439.24) * mm});
            skLineSegment(sketch, "E347", {"start": v(-1108.72, -439.24) * mm, "end": v(-1090.55, -435.67) * mm});
            skLineSegment(sketch, "E348", {"start": v(-1090.55, -435.67) * mm, "end": v(-1076.98, -432) * mm});
            skLineSegment(sketch, "E349", {"start": v(-1076.98, -432) * mm, "end": v(-1063.06, -427.18) * mm});
            skLineSegment(sketch, "E350", {"start": v(-1063.06, -427.18) * mm, "end": v(-1053, -425.53) * mm});
            skLineSegment(sketch, "E351", {"start": v(-1053, -425.53) * mm, "end": v(-1046.86, -427.08) * mm});
            skLineSegment(sketch, "E352", {"start": v(-1046.86, -427.08) * mm, "end": v(-1017.94, -477.17) * mm});
            skLineSegment(sketch, "E353", {"start": v(-1017.94, -477.17) * mm, "end": v(-1019.66, -483.27) * mm});
            skLineSegment(sketch, "E354", {"start": v(-1019.66, -483.27) * mm, "end": v(-1026.12, -491.16) * mm});
            skLineSegment(sketch, "E355", {"start": v(-1026.12, -491.16) * mm, "end": v(-1037.26, -500.8) * mm});
            skLineSegment(sketch, "E356", {"start": v(-1037.26, -500.8) * mm, "end": v(-1047.22, -510.72) * mm});
            skLineSegment(sketch, "E357", {"start": v(-1047.22, -510.72) * mm, "end": v(-1059.4, -524.67) * mm});
            skLineSegment(sketch, "E358", {"start": v(-1059.4, -524.67) * mm, "end": v(-1073.28, -543.02) * mm});
            skLineSegment(sketch, "E359", {"start": v(-1073.28, -543.02) * mm, "end": v(-1088.3, -566.03) * mm});
            skLineSegment(sketch, "E360", {"start": v(-1088.3, -566.03) * mm, "end": v(-1100.15, -587.32) * mm});
            skLineSegment(sketch, "E361", {"start": v(-1100.15, -587.32) * mm, "end": v(-1086.53, -608.3) * mm});
            skLineSegment(sketch, "E362", {"start": v(-1086.53, -608.3) * mm, "end": v(-1070.79, -627.73) * mm});
            skLineSegment(sketch, "E363", {"start": v(-1070.79, -627.73) * mm, "end": v(-1046.88, -623.03) * mm});
            skLineSegment(sketch, "E364", {"start": v(-1046.88, -623.03) * mm, "end": v(-1020.35, -615.87) * mm});
            skLineSegment(sketch, "E365", {"start": v(-1020.35, -615.87) * mm, "end": v(-998.62, -608.33) * mm});
            skLineSegment(sketch, "E366", {"start": v(-998.62, -608.33) * mm, "end": v(-981.58, -601.06) * mm});
            skLineSegment(sketch, "E367", {"start": v(-981.58, -601.06) * mm, "end": v(-969.07, -594.65) * mm});
            skLineSegment(sketch, "E368", {"start": v(-969.07, -594.65) * mm, "end": v(-956.46, -587.04) * mm});
            skLineSegment(sketch, "E369", {"start": v(-956.46, -587.04) * mm, "end": v(-946.96, -583.33) * mm});
            skLineSegment(sketch, "E370", {"start": v(-946.96, -583.33) * mm, "end": v(-940.63, -583.58) * mm});
            skLineSegment(sketch, "E371", {"start": v(-940.63, -583.58) * mm, "end": v(-901.93, -626.56) * mm});
            skLineSegment(sketch, "E372", {"start": v(-901.93, -626.56) * mm, "end": v(-902.35, -632.88) * mm});
            skLineSegment(sketch, "E373", {"start": v(-902.35, -632.88) * mm, "end": v(-907.03, -641.94) * mm});
            skLineSegment(sketch, "E374", {"start": v(-907.03, -641.94) * mm, "end": v(-915.92, -653.69) * mm});
            skLineSegment(sketch, "E375", {"start": v(-915.92, -653.69) * mm, "end": v(-923.6, -665.46) * mm});
            skLineSegment(sketch, "E376", {"start": v(-923.6, -665.46) * mm, "end": v(-932.61, -681.64) * mm});
            skLineSegment(sketch, "E377", {"start": v(-932.61, -681.64) * mm, "end": v(-942.38, -702.47) * mm});
            skLineSegment(sketch, "E378", {"start": v(-942.38, -702.47) * mm, "end": v(-952.28, -728.1) * mm});
            skLineSegment(sketch, "E379", {"start": v(-952.28, -728.1) * mm, "end": v(-959.45, -751.39) * mm});
            skLineSegment(sketch, "E380", {"start": v(-959.45, -751.39) * mm, "end": v(-941.76, -769.07) * mm});
            skLineSegment(sketch, "E381", {"start": v(-941.76, -769.07) * mm, "end": v(-922.32, -784.81) * mm});
            skLineSegment(sketch, "E382", {"start": v(-922.32, -784.81) * mm, "end": v(-899.92, -775.25) * mm});
            skLineSegment(sketch, "E383", {"start": v(-899.92, -775.25) * mm, "end": v(-875.46, -762.72) * mm});
            skLineSegment(sketch, "E384", {"start": v(-875.46, -762.72) * mm, "end": v(-855.77, -750.83) * mm});
            skLineSegment(sketch, "E385", {"start": v(-855.77, -750.83) * mm, "end": v(-840.61, -740.18) * mm});
            skLineSegment(sketch, "E386", {"start": v(-840.61, -740.18) * mm, "end": v(-829.71, -731.31) * mm});
            skLineSegment(sketch, "E387", {"start": v(-829.71, -731.31) * mm, "end": v(-818.95, -721.24) * mm});
            skLineSegment(sketch, "E388", {"start": v(-818.95, -721.24) * mm, "end": v(-810.44, -715.64) * mm});
            skLineSegment(sketch, "E389", {"start": v(-810.44, -715.64) * mm, "end": v(-804.2, -714.56) * mm});
            skLineSegment(sketch, "E390", {"start": v(-804.2, -714.56) * mm, "end": v(-757.4, -748.56) * mm});
            skLineSegment(sketch, "E391", {"start": v(-757.4, -748.56) * mm, "end": v(-756.5, -754.83) * mm});
            skLineSegment(sketch, "E392", {"start": v(-756.5, -754.83) * mm, "end": v(-759.19, -764.66) * mm});
            skLineSegment(sketch, "E393", {"start": v(-759.19, -764.66) * mm, "end": v(-765.44, -778) * mm});
            skLineSegment(sketch, "E394", {"start": v(-765.44, -778) * mm, "end": v(-770.5, -791.11) * mm});
            skLineSegment(sketch, "E395", {"start": v(-770.5, -791.11) * mm, "end": v(-775.96, -808.82) * mm});
            skLineSegment(sketch, "E396", {"start": v(-775.96, -808.82) * mm, "end": v(-781.18, -831.22) * mm});
            skLineSegment(sketch, "E397", {"start": v(-781.18, -831.22) * mm, "end": v(-785.53, -858.35) * mm});
            skLineSegment(sketch, "E398", {"start": v(-785.53, -858.35) * mm, "end": v(-787.7, -882.62) * mm});
            skLineSegment(sketch, "E399", {"start": v(-787.7, -882.62) * mm, "end": v(-766.73, -896.24) * mm});
            skLineSegment(sketch, "E400", {"start": v(-766.73, -896.24) * mm, "end": v(-744.44, -907.6) * mm});
            skLineSegment(sketch, "E401", {"start": v(-744.44, -907.6) * mm, "end": v(-724.52, -893.58) * mm});
            skLineSegment(sketch, "E402", {"start": v(-724.52, -893.58) * mm, "end": v(-703.2, -876.24) * mm});
            skLineSegment(sketch, "E403", {"start": v(-703.2, -876.24) * mm, "end": v(-686.4, -860.52) * mm});
            skLineSegment(sketch, "E404", {"start": v(-686.4, -860.52) * mm, "end": v(-673.8, -846.94) * mm});
            skLineSegment(sketch, "E405", {"start": v(-673.8, -846.94) * mm, "end": v(-664.98, -836) * mm});
            skLineSegment(sketch, "E406", {"start": v(-664.98, -836) * mm, "end": v(-656.55, -823.92) * mm});
            skLineSegment(sketch, "E407", {"start": v(-656.55, -823.92) * mm, "end": v(-649.38, -816.67) * mm});
            skLineSegment(sketch, "E408", {"start": v(-649.38, -816.67) * mm, "end": v(-643.5, -814.32) * mm});
            skLineSegment(sketch, "E409", {"start": v(-643.5, -814.32) * mm, "end": v(-590.66, -837.84) * mm});
            skLineSegment(sketch, "E410", {"start": v(-590.66, -837.84) * mm, "end": v(-588.47, -843.79) * mm});
            skLineSegment(sketch, "E411", {"start": v(-588.47, -843.79) * mm, "end": v(-589.06, -853.97) * mm});
            skLineSegment(sketch, "E412", {"start": v(-589.06, -853.97) * mm, "end": v(-592.4, -868.32) * mm});
            skLineSegment(sketch, "E413", {"start": v(-592.4, -868.32) * mm, "end": v(-594.63, -882.2) * mm});
            skLineSegment(sketch, "E414", {"start": v(-594.63, -882.2) * mm, "end": v(-596.29, -900.64) * mm});
            skLineSegment(sketch, "E415", {"start": v(-596.29, -900.64) * mm, "end": v(-596.74, -923.64) * mm});
            skLineSegment(sketch, "E416", {"start": v(-596.74, -923.64) * mm, "end": v(-595.35, -951.09) * mm});
            skLineSegment(sketch, "E417", {"start": v(-595.35, -951.09) * mm, "end": v(-592.43, -975.27) * mm});
            skLineSegment(sketch, "E418", {"start": v(-592.43, -975.27) * mm, "end": v(-569.08, -984.24) * mm});
            skLineSegment(sketch, "E419", {"start": v(-569.08, -984.24) * mm, "end": v(-544.92, -990.71) * mm});
            skLineSegment(sketch, "E420", {"start": v(-544.92, -990.71) * mm, "end": v(-528.35, -972.86) * mm});
            skLineSegment(sketch, "E421", {"start": v(-528.35, -972.86) * mm, "end": v(-511.1, -951.47) * mm});
            skLineSegment(sketch, "E422", {"start": v(-511.1, -951.47) * mm, "end": v(-497.94, -932.6) * mm});
            skLineSegment(sketch, "E423", {"start": v(-497.94, -932.6) * mm, "end": v(-488.43, -916.7) * mm});
            skLineSegment(sketch, "E424", {"start": v(-488.43, -916.7) * mm, "end": v(-482.08, -904.17) * mm});
            skLineSegment(sketch, "E425", {"start": v(-482.08, -904.17) * mm, "end": v(-476.35, -890.59) * mm});
            skLineSegment(sketch, "E426", {"start": v(-476.35, -890.59) * mm, "end": v(-470.85, -882) * mm});
            skLineSegment(sketch, "E427", {"start": v(-470.85, -882) * mm, "end": v(-465.58, -878.49) * mm});
            skLineSegment(sketch, "E428", {"start": v(-465.58, -878.49) * mm, "end": v(-409, -890.51) * mm});
            skLineSegment(sketch, "E429", {"start": v(-409, -890.51) * mm, "end": v(-405.62, -895.87) * mm});
            skLineSegment(sketch, "E430", {"start": v(-405.62, -895.87) * mm, "end": v(-404.09, -905.95) * mm});
            skLineSegment(sketch, "E431", {"start": v(-404.09, -905.95) * mm, "end": v(-404.38, -920.68) * mm});
            skLineSegment(sketch, "E432", {"start": v(-404.38, -920.68) * mm, "end": v(-403.67, -934.72) * mm});
            skLineSegment(sketch, "E433", {"start": v(-403.67, -934.72) * mm, "end": v(-401.45, -953.1) * mm});
            skLineSegment(sketch, "E434", {"start": v(-401.45, -953.1) * mm, "end": v(-397.1, -975.7) * mm});
            skLineSegment(sketch, "E435", {"start": v(-397.1, -975.7) * mm, "end": v(-390.05, -1002.25) * mm});
            skLineSegment(sketch, "E436", {"start": v(-390.05, -1002.25) * mm, "end": v(-382.16, -1025.3) * mm});
            skLineSegment(sketch, "E437", {"start": v(-382.16, -1025.3) * mm, "end": v(-357.46, -1029.22) * mm});
            skLineSegment(sketch, "E438", {"start": v(-357.46, -1029.22) * mm, "end": v(-332.48, -1030.53) * mm});
            skLineSegment(sketch, "E439", {"start": v(-332.48, -1030.53) * mm, "end": v(-319.98, -1009.62) * mm});
            skLineSegment(sketch, "E440", {"start": v(-319.98, -1009.62) * mm, "end": v(-307.55, -985.11) * mm});
            skLineSegment(sketch, "E441", {"start": v(-307.55, -985.11) * mm, "end": v(-298.6, -963.92) * mm});
            skLineSegment(sketch, "E442", {"start": v(-298.6, -963.92) * mm, "end": v(-292.61, -946.39) * mm});
            skLineSegment(sketch, "E443", {"start": v(-292.61, -946.39) * mm, "end": v(-289, -932.8) * mm});
            skLineSegment(sketch, "E444", {"start": v(-289, -932.8) * mm, "end": v(-286.22, -918.34) * mm});
            skLineSegment(sketch, "E445", {"start": v(-286.22, -918.34) * mm, "end": v(-282.62, -908.8) * mm});
            skLineSegment(sketch, "E446", {"start": v(-282.62, -908.8) * mm, "end": v(-278.2, -904.26) * mm});
            skLineSegment(sketch, "E447", {"start": v(-278.2, -904.26) * mm, "end": v(-220.37, -904.26) * mm});
            skLineSegment(sketch, "E448", {"start": v(-220.37, -904.26) * mm, "end": v(-215.95, -908.8) * mm});
            skLineSegment(sketch, "E449", {"start": v(-215.95, -908.8) * mm, "end": v(-212.35, -918.34) * mm});
            skLineSegment(sketch, "E450", {"start": v(-212.35, -918.34) * mm, "end": v(-209.57, -932.8) * mm});
            skLineSegment(sketch, "E451", {"start": v(-209.57, -932.8) * mm, "end": v(-205.96, -946.39) * mm});
            skLineSegment(sketch, "E452", {"start": v(-205.96, -946.39) * mm, "end": v(-199.96, -963.92) * mm});
            skLineSegment(sketch, "E453", {"start": v(-199.96, -963.92) * mm, "end": v(-191.02, -985.11) * mm});
            skLineSegment(sketch, "E454", {"start": v(-191.02, -985.11) * mm, "end": v(-178.6, -1009.62) * mm});
            skLineSegment(sketch, "E455", {"start": v(-178.6, -1009.62) * mm, "end": v(-166.09, -1030.53) * mm});
            skLineSegment(sketch, "E456", {"start": v(-166.09, -1030.53) * mm, "end": v(-141.11, -1029.22) * mm});
            skLineSegment(sketch, "E457", {"start": v(-141.11, -1029.22) * mm, "end": v(-116.4, -1025.3) * mm});
            skLineSegment(sketch, "E458", {"start": v(-116.4, -1025.3) * mm, "end": v(-108.52, -1002.25) * mm});
            skLineSegment(sketch, "E459", {"start": v(-108.52, -1002.25) * mm, "end": v(-101.46, -975.7) * mm});
            skLineSegment(sketch, "E460", {"start": v(-101.46, -975.7) * mm, "end": v(-97.12, -953.1) * mm});
            skLineSegment(sketch, "E461", {"start": v(-97.12, -953.1) * mm, "end": v(-94.9, -934.72) * mm});
            skLineSegment(sketch, "E462", {"start": v(-94.9, -934.72) * mm, "end": v(-94.2, -920.68) * mm});
            skLineSegment(sketch, "E463", {"start": v(-94.2, -920.68) * mm, "end": v(-94.48, -905.95) * mm});
            skLineSegment(sketch, "E464", {"start": v(-94.48, -905.95) * mm, "end": v(-92.95, -895.87) * mm});
            skLineSegment(sketch, "E465", {"start": v(-92.95, -895.87) * mm, "end": v(-89.57, -890.51) * mm});
            skLineSegment(sketch, "E466", {"start": v(-89.57, -890.51) * mm, "end": v(-33, -878.49) * mm});
            skLineSegment(sketch, "E467", {"start": v(-33, -878.49) * mm, "end": v(-27.73, -882) * mm});
            skLineSegment(sketch, "E468", {"start": v(-27.73, -882) * mm, "end": v(-22.22, -890.59) * mm});
            skLineSegment(sketch, "E469", {"start": v(-22.22, -890.59) * mm, "end": v(-16.5, -904.17) * mm});
            skLineSegment(sketch, "E470", {"start": v(-16.5, -904.17) * mm, "end": v(-10.14, -916.7) * mm});
            skLineSegment(sketch, "E471", {"start": v(-10.14, -916.7) * mm, "end": v(-0.63, -932.6) * mm});
            skLineSegment(sketch, "E472", {"start": v(-0.63, -932.6) * mm, "end": v(12.53, -951.47) * mm});
            skLineSegment(sketch, "E473", {"start": v(12.53, -951.47) * mm, "end": v(29.77, -972.86) * mm});
            skLineSegment(sketch, "E474", {"start": v(29.77, -972.86) * mm, "end": v(46.35, -990.71) * mm});
            skLineSegment(sketch, "E475", {"start": v(46.35, -990.71) * mm, "end": v(70.51, -984.24) * mm});
            skLineSegment(sketch, "E476", {"start": v(70.51, -984.24) * mm, "end": v(93.86, -975.27) * mm});
            skLineSegment(sketch, "E477", {"start": v(93.86, -975.27) * mm, "end": v(96.78, -951.09) * mm});
            skLineSegment(sketch, "E478", {"start": v(96.78, -951.09) * mm, "end": v(98.16, -923.64) * mm});
            skLineSegment(sketch, "E479", {"start": v(98.16, -923.64) * mm, "end": v(97.72, -900.64) * mm});
            skLineSegment(sketch, "E480", {"start": v(97.72, -900.64) * mm, "end": v(96.06, -882.2) * mm});
            skLineSegment(sketch, "E481", {"start": v(96.06, -882.2) * mm, "end": v(93.84, -868.32) * mm});
            skLineSegment(sketch, "E482", {"start": v(93.84, -868.32) * mm, "end": v(90.5, -853.97) * mm});
            skLineSegment(sketch, "E483", {"start": v(90.5, -853.97) * mm, "end": v(89.9, -843.79) * mm});
            skLineSegment(sketch, "E484", {"start": v(89.9, -843.79) * mm, "end": v(92.1, -837.84) * mm});
            skLineSegment(sketch, "E485", {"start": v(92.1, -837.84) * mm, "end": v(144.93, -814.32) * mm});
            skLineSegment(sketch, "E486", {"start": v(144.93, -814.32) * mm, "end": v(150.81, -816.67) * mm});
            skLineSegment(sketch, "E487", {"start": v(150.81, -816.67) * mm, "end": v(157.98, -823.92) * mm});
            skLineSegment(sketch, "E488", {"start": v(157.98, -823.92) * mm, "end": v(166.4, -836) * mm});
            skLineSegment(sketch, "E489", {"start": v(166.4, -836) * mm, "end": v(175.23, -846.94) * mm});
            skLineSegment(sketch, "E490", {"start": v(175.23, -846.94) * mm, "end": v(187.83, -860.52) * mm});
            skLineSegment(sketch, "E491", {"start": v(187.83, -860.52) * mm, "end": v(204.63, -876.24) * mm});
            skLineSegment(sketch, "E492", {"start": v(204.63, -876.24) * mm, "end": v(225.94, -893.58) * mm});
            skLineSegment(sketch, "E493", {"start": v(225.94, -893.58) * mm, "end": v(245.87, -907.6) * mm});
            skLineSegment(sketch, "E494", {"start": v(245.87, -907.6) * mm, "end": v(268.16, -896.24) * mm});
            skLineSegment(sketch, "E495", {"start": v(268.16, -896.24) * mm, "end": v(289.14, -882.62) * mm});
            skLineSegment(sketch, "E496", {"start": v(289.14, -882.62) * mm, "end": v(286.96, -858.35) * mm});
            skLineSegment(sketch, "E497", {"start": v(286.96, -858.35) * mm, "end": v(282.6, -831.22) * mm});
            skLineSegment(sketch, "E498", {"start": v(282.6, -831.22) * mm, "end": v(277.39, -808.82) * mm});
            skLineSegment(sketch, "E499", {"start": v(277.39, -808.82) * mm, "end": v(271.93, -791.11) * mm});
            skLineSegment(sketch, "E500", {"start": v(271.93, -791.11) * mm, "end": v(266.87, -778) * mm});
            skLineSegment(sketch, "E501", {"start": v(266.87, -778) * mm, "end": v(260.62, -764.66) * mm});
            skLineSegment(sketch, "E502", {"start": v(260.62, -764.66) * mm, "end": v(257.92, -754.83) * mm});
            skLineSegment(sketch, "E503", {"start": v(257.92, -754.83) * mm, "end": v(258.83, -748.56) * mm});
            skLineSegment(sketch, "E504", {"start": v(258.83, -748.56) * mm, "end": v(305.62, -714.56) * mm});
            skLineSegment(sketch, "E505", {"start": v(305.62, -714.56) * mm, "end": v(311.86, -715.64) * mm});
            skLineSegment(sketch, "E506", {"start": v(311.86, -715.64) * mm, "end": v(320.38, -721.24) * mm});
            skLineSegment(sketch, "E507", {"start": v(320.38, -721.24) * mm, "end": v(331.14, -731.31) * mm});
            skLineSegment(sketch, "E508", {"start": v(331.14, -731.31) * mm, "end": v(342.04, -740.18) * mm});
            skLineSegment(sketch, "E509", {"start": v(342.04, -740.18) * mm, "end": v(357.2, -750.83) * mm});
            skLineSegment(sketch, "E510", {"start": v(357.2, -750.83) * mm, "end": v(376.89, -762.72) * mm});
            skLineSegment(sketch, "E511", {"start": v(376.89, -762.72) * mm, "end": v(401.35, -775.25) * mm});
            skLineSegment(sketch, "E512", {"start": v(401.35, -775.25) * mm, "end": v(423.75, -784.81) * mm});
            skLineSegment(sketch, "E513", {"start": v(423.75, -784.81) * mm, "end": v(443.2, -769.07) * mm});
            skLineSegment(sketch, "E514", {"start": v(443.2, -769.07) * mm, "end": v(460.88, -751.39) * mm});
            skLineSegment(sketch, "E515", {"start": v(460.88, -751.39) * mm, "end": v(453.7, -728.1) * mm});
            skLineSegment(sketch, "E516", {"start": v(453.7, -728.1) * mm, "end": v(443.8, -702.47) * mm});
            skLineSegment(sketch, "E517", {"start": v(443.8, -702.47) * mm, "end": v(434.04, -681.64) * mm});
            skLineSegment(sketch, "E518", {"start": v(434.04, -681.64) * mm, "end": v(425.03, -665.46) * mm});
            skLineSegment(sketch, "E519", {"start": v(425.03, -665.46) * mm, "end": v(417.35, -653.69) * mm});
            skLineSegment(sketch, "E520", {"start": v(417.35, -653.69) * mm, "end": v(408.45, -641.94) * mm});
            skLineSegment(sketch, "E521", {"start": v(408.45, -641.94) * mm, "end": v(403.77, -632.88) * mm});
            skLineSegment(sketch, "E522", {"start": v(403.77, -632.88) * mm, "end": v(403.36, -626.56) * mm});
            skLineSegment(sketch, "E523", {"start": v(403.36, -626.56) * mm, "end": v(442.06, -583.58) * mm});
            skLineSegment(sketch, "E524", {"start": v(442.06, -583.58) * mm, "end": v(448.4, -583.33) * mm});
            skLineSegment(sketch, "E525", {"start": v(448.4, -583.33) * mm, "end": v(457.89, -587.04) * mm});
            skLineSegment(sketch, "E526", {"start": v(457.89, -587.04) * mm, "end": v(470.5, -594.65) * mm});
            skLineSegment(sketch, "E527", {"start": v(470.5, -594.65) * mm, "end": v(483.01, -601.06) * mm});
            skLineSegment(sketch, "E528", {"start": v(483.01, -601.06) * mm, "end": v(500.05, -608.33) * mm});
            skLineSegment(sketch, "E529", {"start": v(500.05, -608.33) * mm, "end": v(521.78, -615.87) * mm});
            skLineSegment(sketch, "E530", {"start": v(521.78, -615.87) * mm, "end": v(548.31, -623.03) * mm});
            skLineSegment(sketch, "E531", {"start": v(548.31, -623.03) * mm, "end": v(572.22, -627.73) * mm});
            skLineSegment(sketch, "E532", {"start": v(572.22, -627.73) * mm, "end": v(587.96, -608.3) * mm});
            skLineSegment(sketch, "E533", {"start": v(587.96, -608.3) * mm, "end": v(601.58, -587.32) * mm});
            skLineSegment(sketch, "E534", {"start": v(601.58, -587.32) * mm, "end": v(589.72, -566.03) * mm});
            skLineSegment(sketch, "E535", {"start": v(589.72, -566.03) * mm, "end": v(574.71, -543.02) * mm});
            skLineSegment(sketch, "E536", {"start": v(574.71, -543.02) * mm, "end": v(560.83, -524.67) * mm});
            skLineSegment(sketch, "E537", {"start": v(560.83, -524.67) * mm, "end": v(548.65, -510.72) * mm});
            skLineSegment(sketch, "E538", {"start": v(548.65, -510.72) * mm, "end": v(538.7, -500.8) * mm});
            skLineSegment(sketch, "E539", {"start": v(538.7, -500.8) * mm, "end": v(527.55, -491.16) * mm});
            skLineSegment(sketch, "E540", {"start": v(527.55, -491.16) * mm, "end": v(521.09, -483.27) * mm});
            skLineSegment(sketch, "E541", {"start": v(521.09, -483.27) * mm, "end": v(519.37, -477.17) * mm});
            skLineSegment(sketch, "E542", {"start": v(519.37, -477.17) * mm, "end": v(548.28, -427.08) * mm});
            skLineSegment(sketch, "E543", {"start": v(548.28, -427.08) * mm, "end": v(554.43, -425.53) * mm});
            skLineSegment(sketch, "E544", {"start": v(554.43, -425.53) * mm, "end": v(564.49, -427.18) * mm});
            skLineSegment(sketch, "E545", {"start": v(564.49, -427.18) * mm, "end": v(578.41, -432) * mm});
            skLineSegment(sketch, "E546", {"start": v(578.41, -432) * mm, "end": v(591.97, -435.67) * mm});
            skLineSegment(sketch, "E547", {"start": v(591.97, -435.67) * mm, "end": v(610.15, -439.24) * mm});
            skLineSegment(sketch, "E548", {"start": v(610.15, -439.24) * mm, "end": v(632.98, -442.1) * mm});
            skLineSegment(sketch, "E549", {"start": v(632.98, -442.1) * mm, "end": v(660.42, -443.59) * mm});
            skLineSegment(sketch, "E550", {"start": v(660.42, -443.59) * mm, "end": v(684.78, -443.21) * mm});
            skLineSegment(sketch, "E551", {"start": v(684.78, -443.21) * mm, "end": v(696.13, -420.93) * mm});
            skLineSegment(sketch, "E552", {"start": v(696.13, -420.93) * mm, "end": v(705.1, -397.58) * mm});
            skLineSegment(sketch, "E553", {"start": v(705.1, -397.58) * mm, "end": v(689.07, -379.22) * mm});
            skLineSegment(sketch, "E554", {"start": v(689.07, -379.22) * mm, "end": v(669.6, -359.83) * mm});
            skLineSegment(sketch, "E555", {"start": v(669.6, -359.83) * mm, "end": v(652.21, -344.78) * mm});
            skLineSegment(sketch, "E556", {"start": v(652.21, -344.78) * mm, "end": v(637.4, -333.66) * mm});
            skLineSegment(sketch, "E557", {"start": v(637.4, -333.66) * mm, "end": v(625.6, -326.03) * mm});
            skLineSegment(sketch, "E558", {"start": v(625.6, -326.03) * mm, "end": v(612.69, -318.91) * mm});
            skLineSegment(sketch, "E559", {"start": v(612.69, -318.91) * mm, "end": v(604.73, -312.54) * mm});
            skLineSegment(sketch, "E560", {"start": v(604.73, -312.54) * mm, "end": v(601.78, -306.93) * mm});
            skLineSegment(sketch, "E561", {"start": v(601.78, -306.93) * mm, "end": v(619.65, -251.93) * mm});
            skLineSegment(sketch, "E562", {"start": v(619.65, -251.93) * mm, "end": v(625.33, -249.13) * mm});
            skLineSegment(sketch, "E563", {"start": v(625.33, -249.13) * mm, "end": v(635.52, -248.65) * mm});
            skLineSegment(sketch, "E564", {"start": v(635.52, -248.65) * mm, "end": v(650.14, -250.48) * mm});
            skLineSegment(sketch, "E565", {"start": v(650.14, -250.48) * mm, "end": v(664.17, -251.24) * mm});
            skLineSegment(sketch, "E566", {"start": v(664.17, -251.24) * mm, "end": v(682.7, -250.96) * mm});
            skLineSegment(sketch, "E567", {"start": v(682.7, -250.96) * mm, "end": v(705.62, -249) * mm});
            skLineSegment(sketch, "E568", {"start": v(705.62, -249) * mm, "end": v(732.77, -244.76) * mm});
            skLineSegment(sketch, "E569", {"start": v(732.77, -244.76) * mm, "end": v(756.52, -239.33) * mm});
            skPoint(sketch, "E570", {"position": v(-249.29, 0) * mm});
            skCircle(sketch, "E571", {"center": v(-249.29, 0) * mm, "radius": 50.8 * mm});
            skSolve(sketch);
        }
        {
            var Q0;
            Q0=makeQuery(id+"F0.imprint","IMPRINT",FACE,{"disambiguationData":[TD([[makeQuery(id+"F0.imprint","IMPRINT",EDGE,{"derivedFrom":sQuery(id+"F0.wireOp",EDGE,"E0")}),1.0]])]});
            extrude(context, id + "F1", {"entities" : qUnion([Q0]), "depth" : 127 * mm, "offsetDistance" : 25.4 * mm});
        }
        {
            var Q0;
            Q0=makeQuery(id+"F1.opExtrude","SWEPT_BODY",BODY,{"disambiguationData":[OSD([sQuery(id+"F0.wireOp",EDGE,"E0"),sQuery(id+"F0.wireOp",EDGE,"E1"),sQuery(id+"F0.wireOp",EDGE,"E2"),sQuery(id+"F0.wireOp",EDGE,"E3"),sQuery(id+"F0.wireOp",EDGE,"E4"),sQuery(id+"F0.wireOp",EDGE,"E5"),sQuery(id+"F0.wireOp",EDGE,"E6"),sQuery(id+"F0.wireOp",EDGE,"E7"),sQuery(id+"F0.wireOp",EDGE,"E8"),sQuery(id+"F0.wireOp",EDGE,"E9"),sQuery(id+"F0.wireOp",EDGE,"E10"),sQuery(id+"F0.wireOp",EDGE,"E11"),sQuery(id+"F0.wireOp",EDGE,"E12"),sQuery(id+"F0.wireOp",EDGE,"E13"),sQuery(id+"F0.wireOp",EDGE,"E14"),sQuery(id+"F0.wireOp",EDGE,"E15"),sQuery(id+"F0.wireOp",EDGE,"E16"),sQuery(id+"F0.wireOp",EDGE,"E17"),sQuery(id+"F0.wireOp",EDGE,"E18"),sQuery(id+"F0.wireOp",EDGE,"E19"),sQuery(id+"F0.wireOp",EDGE,"E20"),sQuery(id+"F0.wireOp",EDGE,"E21"),sQuery(id+"F0.wireOp",EDGE,"E22"),sQuery(id+"F0.wireOp",EDGE,"E23"),sQuery(id+"F0.wireOp",EDGE,"E24"),sQuery(id+"F0.wireOp",EDGE,"E25"),sQuery(id+"F0.wireOp",EDGE,"E26"),sQuery(id+"F0.wireOp",EDGE,"E27"),sQuery(id+"F0.wireOp",EDGE,"E28"),sQuery(id+"F0.wireOp",EDGE,"E29"),sQuery(id+"F0.wireOp",EDGE,"E30"),sQuery(id+"F0.wireOp",EDGE,"E31"),sQuery(id+"F0.wireOp",EDGE,"E32"),sQuery(id+"F0.wireOp",EDGE,"E33"),sQuery(id+"F0.wireOp",EDGE,"E34"),sQuery(id+"F0.wireOp",EDGE,"E35"),sQuery(id+"F0.wireOp",EDGE,"E36"),sQuery(id+"F0.wireOp",EDGE,"E37"),sQuery(id+"F0.wireOp",EDGE,"E38"),sQuery(id+"F0.wireOp",EDGE,"E39"),sQuery(id+"F0.wireOp",EDGE,"E40"),sQuery(id+"F0.wireOp",EDGE,"E41"),sQuery(id+"F0.wireOp",EDGE,"E42"),sQuery(id+"F0.wireOp",EDGE,"E43"),sQuery(id+"F0.wireOp",EDGE,"E44"),sQuery(id+"F0.wireOp",EDGE,"E45"),sQuery(id+"F0.wireOp",EDGE,"E46"),sQuery(id+"F0.wireOp",EDGE,"E47"),sQuery(id+"F0.wireOp",EDGE,"E48"),sQuery(id+"F0.wireOp",EDGE,"E49"),sQuery(id+"F0.wireOp",EDGE,"E50"),sQuery(id+"F0.wireOp",EDGE,"E51"),sQuery(id+"F0.wireOp",EDGE,"E52"),sQuery(id+"F0.wireOp",EDGE,"E53"),sQuery(id+"F0.wireOp",EDGE,"E54"),sQuery(id+"F0.wireOp",EDGE,"E55"),sQuery(id+"F0.wireOp",EDGE,"E56"),sQuery(id+"F0.wireOp",EDGE,"E57"),sQuery(id+"F0.wireOp",EDGE,"E58"),sQuery(id+"F0.wireOp",EDGE,"E59"),sQuery(id+"F0.wireOp",EDGE,"E60"),sQuery(id+"F0.wireOp",EDGE,"E61"),sQuery(id+"F0.wireOp",EDGE,"E62"),sQuery(id+"F0.wireOp",EDGE,"E63"),sQuery(id+"F0.wireOp",EDGE,"E64"),sQuery(id+"F0.wireOp",EDGE,"E65"),sQuery(id+"F0.wireOp",EDGE,"E66"),sQuery(id+"F0.wireOp",EDGE,"E67"),sQuery(id+"F0.wireOp",EDGE,"E68"),sQuery(id+"F0.wireOp",EDGE,"E69"),sQuery(id+"F0.wireOp",EDGE,"E70"),sQuery(id+"F0.wireOp",EDGE,"E71"),sQuery(id+"F0.wireOp",EDGE,"E72"),sQuery(id+"F0.wireOp",EDGE,"E73"),sQuery(id+"F0.wireOp",EDGE,"E74"),sQuery(id+"F0.wireOp",EDGE,"E75"),sQuery(id+"F0.wireOp",EDGE,"E76"),sQuery(id+"F0.wireOp",EDGE,"E77"),sQuery(id+"F0.wireOp",EDGE,"E78"),sQuery(id+"F0.wireOp",EDGE,"E79"),sQuery(id+"F0.wireOp",EDGE,"E80"),sQuery(id+"F0.wireOp",EDGE,"E81"),sQuery(id+"F0.wireOp",EDGE,"E82"),sQuery(id+"F0.wireOp",EDGE,"E83"),sQuery(id+"F0.wireOp",EDGE,"E84"),sQuery(id+"F0.wireOp",EDGE,"E85"),sQuery(id+"F0.wireOp",EDGE,"E86"),sQuery(id+"F0.wireOp",EDGE,"E87"),sQuery(id+"F0.wireOp",EDGE,"E88"),sQuery(id+"F0.wireOp",EDGE,"E89"),sQuery(id+"F0.wireOp",EDGE,"E90"),sQuery(id+"F0.wireOp",EDGE,"E91"),sQuery(id+"F0.wireOp",EDGE,"E92"),sQuery(id+"F0.wireOp",EDGE,"E93"),sQuery(id+"F0.wireOp",EDGE,"E94"),sQuery(id+"F0.wireOp",EDGE,"E95"),sQuery(id+"F0.wireOp",EDGE,"E96"),sQuery(id+"F0.wireOp",EDGE,"E97"),sQuery(id+"F0.wireOp",EDGE,"E98"),sQuery(id+"F0.wireOp",EDGE,"E99"),sQuery(id+"F0.wireOp",EDGE,"E100"),sQuery(id+"F0.wireOp",EDGE,"E101"),sQuery(id+"F0.wireOp",EDGE,"E102"),sQuery(id+"F0.wireOp",EDGE,"E103"),sQuery(id+"F0.wireOp",EDGE,"E104"),sQuery(id+"F0.wireOp",EDGE,"E105"),sQuery(id+"F0.wireOp",EDGE,"E106"),sQuery(id+"F0.wireOp",EDGE,"E107"),sQuery(id+"F0.wireOp",EDGE,"E108"),sQuery(id+"F0.wireOp",EDGE,"E109"),sQuery(id+"F0.wireOp",EDGE,"E110"),sQuery(id+"F0.wireOp",EDGE,"E111"),sQuery(id+"F0.wireOp",EDGE,"E112"),sQuery(id+"F0.wireOp",EDGE,"E113"),sQuery(id+"F0.wireOp",EDGE,"E114"),sQuery(id+"F0.wireOp",EDGE,"E115"),sQuery(id+"F0.wireOp",EDGE,"E116"),sQuery(id+"F0.wireOp",EDGE,"E117"),sQuery(id+"F0.wireOp",EDGE,"E118"),sQuery(id+"F0.wireOp",EDGE,"E119"),sQuery(id+"F0.wireOp",EDGE,"E120"),sQuery(id+"F0.wireOp",EDGE,"E121"),sQuery(id+"F0.wireOp",EDGE,"E122"),sQuery(id+"F0.wireOp",EDGE,"E123"),sQuery(id+"F0.wireOp",EDGE,"E124"),sQuery(id+"F0.wireOp",EDGE,"E125"),sQuery(id+"F0.wireOp",EDGE,"E126"),sQuery(id+"F0.wireOp",EDGE,"E127"),sQuery(id+"F0.wireOp",EDGE,"E128"),sQuery(id+"F0.wireOp",EDGE,"E129"),sQuery(id+"F0.wireOp",EDGE,"E130"),sQuery(id+"F0.wireOp",EDGE,"E131"),sQuery(id+"F0.wireOp",EDGE,"E132"),sQuery(id+"F0.wireOp",EDGE,"E133"),sQuery(id+"F0.wireOp",EDGE,"E134"),sQuery(id+"F0.wireOp",EDGE,"E135"),sQuery(id+"F0.wireOp",EDGE,"E136"),sQuery(id+"F0.wireOp",EDGE,"E137"),sQuery(id+"F0.wireOp",EDGE,"E138"),sQuery(id+"F0.wireOp",EDGE,"E139"),sQuery(id+"F0.wireOp",EDGE,"E140"),sQuery(id+"F0.wireOp",EDGE,"E141"),sQuery(id+"F0.wireOp",EDGE,"E142"),sQuery(id+"F0.wireOp",EDGE,"E143"),sQuery(id+"F0.wireOp",EDGE,"E144"),sQuery(id+"F0.wireOp",EDGE,"E145"),sQuery(id+"F0.wireOp",EDGE,"E146"),sQuery(id+"F0.wireOp",EDGE,"E147"),sQuery(id+"F0.wireOp",EDGE,"E148"),sQuery(id+"F0.wireOp",EDGE,"E149"),sQuery(id+"F0.wireOp",EDGE,"E150"),sQuery(id+"F0.wireOp",EDGE,"E151"),sQuery(id+"F0.wireOp",EDGE,"E152"),sQuery(id+"F0.wireOp",EDGE,"E153"),sQuery(id+"F0.wireOp",EDGE,"E154"),sQuery(id+"F0.wireOp",EDGE,"E155"),sQuery(id+"F0.wireOp",EDGE,"E156"),sQuery(id+"F0.wireOp",EDGE,"E157"),sQuery(id+"F0.wireOp",EDGE,"E158"),sQuery(id+"F0.wireOp",EDGE,"E159"),sQuery(id+"F0.wireOp",EDGE,"E160"),sQuery(id+"F0.wireOp",EDGE,"E161"),sQuery(id+"F0.wireOp",EDGE,"E162"),sQuery(id+"F0.wireOp",EDGE,"E163"),sQuery(id+"F0.wireOp",EDGE,"E164"),sQuery(id+"F0.wireOp",EDGE,"E165"),sQuery(id+"F0.wireOp",EDGE,"E166"),sQuery(id+"F0.wireOp",EDGE,"E167"),sQuery(id+"F0.wireOp",EDGE,"E168"),sQuery(id+"F0.wireOp",EDGE,"E169"),sQuery(id+"F0.wireOp",EDGE,"E170"),sQuery(id+"F0.wireOp",EDGE,"E171"),sQuery(id+"F0.wireOp",EDGE,"E172"),sQuery(id+"F0.wireOp",EDGE,"E173"),sQuery(id+"F0.wireOp",EDGE,"E174"),sQuery(id+"F0.wireOp",EDGE,"E175"),sQuery(id+"F0.wireOp",EDGE,"E176"),sQuery(id+"F0.wireOp",EDGE,"E177"),sQuery(id+"F0.wireOp",EDGE,"E178"),sQuery(id+"F0.wireOp",EDGE,"E179"),sQuery(id+"F0.wireOp",EDGE,"E180"),sQuery(id+"F0.wireOp",EDGE,"E181"),sQuery(id+"F0.wireOp",EDGE,"E182"),sQuery(id+"F0.wireOp",EDGE,"E183"),sQuery(id+"F0.wireOp",EDGE,"E184"),sQuery(id+"F0.wireOp",EDGE,"E185"),sQuery(id+"F0.wireOp",EDGE,"E186"),sQuery(id+"F0.wireOp",EDGE,"E187"),sQuery(id+"F0.wireOp",EDGE,"E188"),sQuery(id+"F0.wireOp",EDGE,"E189"),sQuery(id+"F0.wireOp",EDGE,"E190"),sQuery(id+"F0.wireOp",EDGE,"E191"),sQuery(id+"F0.wireOp",EDGE,"E192"),sQuery(id+"F0.wireOp",EDGE,"E193"),sQuery(id+"F0.wireOp",EDGE,"E194"),sQuery(id+"F0.wireOp",EDGE,"E195"),sQuery(id+"F0.wireOp",EDGE,"E196"),sQuery(id+"F0.wireOp",EDGE,"E197"),sQuery(id+"F0.wireOp",EDGE,"E198"),sQuery(id+"F0.wireOp",EDGE,"E199"),sQuery(id+"F0.wireOp",EDGE,"E200"),sQuery(id+"F0.wireOp",EDGE,"E201"),sQuery(id+"F0.wireOp",EDGE,"E202"),sQuery(id+"F0.wireOp",EDGE,"E203"),sQuery(id+"F0.wireOp",EDGE,"E204"),sQuery(id+"F0.wireOp",EDGE,"E205"),sQuery(id+"F0.wireOp",EDGE,"E206"),sQuery(id+"F0.wireOp",EDGE,"E207"),sQuery(id+"F0.wireOp",EDGE,"E208"),sQuery(id+"F0.wireOp",EDGE,"E209"),sQuery(id+"F0.wireOp",EDGE,"E210"),sQuery(id+"F0.wireOp",EDGE,"E211"),sQuery(id+"F0.wireOp",EDGE,"E212"),sQuery(id+"F0.wireOp",EDGE,"E213"),sQuery(id+"F0.wireOp",EDGE,"E214"),sQuery(id+"F0.wireOp",EDGE,"E215"),sQuery(id+"F0.wireOp",EDGE,"E216"),sQuery(id+"F0.wireOp",EDGE,"E217"),sQuery(id+"F0.wireOp",EDGE,"E218"),sQuery(id+"F0.wireOp",EDGE,"E219"),sQuery(id+"F0.wireOp",EDGE,"E220"),sQuery(id+"F0.wireOp",EDGE,"E221"),sQuery(id+"F0.wireOp",EDGE,"E222"),sQuery(id+"F0.wireOp",EDGE,"E223"),sQuery(id+"F0.wireOp",EDGE,"E224"),sQuery(id+"F0.wireOp",EDGE,"E225"),sQuery(id+"F0.wireOp",EDGE,"E226"),sQuery(id+"F0.wireOp",EDGE,"E227"),sQuery(id+"F0.wireOp",EDGE,"E228"),sQuery(id+"F0.wireOp",EDGE,"E229"),sQuery(id+"F0.wireOp",EDGE,"E230"),sQuery(id+"F0.wireOp",EDGE,"E231"),sQuery(id+"F0.wireOp",EDGE,"E232"),sQuery(id+"F0.wireOp",EDGE,"E233"),sQuery(id+"F0.wireOp",EDGE,"E234"),sQuery(id+"F0.wireOp",EDGE,"E235"),sQuery(id+"F0.wireOp",EDGE,"E236"),sQuery(id+"F0.wireOp",EDGE,"E237"),sQuery(id+"F0.wireOp",EDGE,"E238"),sQuery(id+"F0.wireOp",EDGE,"E239"),sQuery(id+"F0.wireOp",EDGE,"E240"),sQuery(id+"F0.wireOp",EDGE,"E241"),sQuery(id+"F0.wireOp",EDGE,"E242"),sQuery(id+"F0.wireOp",EDGE,"E243"),sQuery(id+"F0.wireOp",EDGE,"E244"),sQuery(id+"F0.wireOp",EDGE,"E245"),sQuery(id+"F0.wireOp",EDGE,"E246"),sQuery(id+"F0.wireOp",EDGE,"E247"),sQuery(id+"F0.wireOp",EDGE,"E248"),sQuery(id+"F0.wireOp",EDGE,"E249"),sQuery(id+"F0.wireOp",EDGE,"E250"),sQuery(id+"F0.wireOp",EDGE,"E251"),sQuery(id+"F0.wireOp",EDGE,"E252"),sQuery(id+"F0.wireOp",EDGE,"E253"),sQuery(id+"F0.wireOp",EDGE,"E254"),sQuery(id+"F0.wireOp",EDGE,"E255"),sQuery(id+"F0.wireOp",EDGE,"E256"),sQuery(id+"F0.wireOp",EDGE,"E257"),sQuery(id+"F0.wireOp",EDGE,"E258"),sQuery(id+"F0.wireOp",EDGE,"E259"),sQuery(id+"F0.wireOp",EDGE,"E260"),sQuery(id+"F0.wireOp",EDGE,"E261"),sQuery(id+"F0.wireOp",EDGE,"E262"),sQuery(id+"F0.wireOp",EDGE,"E263"),sQuery(id+"F0.wireOp",EDGE,"E264"),sQuery(id+"F0.wireOp",EDGE,"E265"),sQuery(id+"F0.wireOp",EDGE,"E266"),sQuery(id+"F0.wireOp",EDGE,"E267"),sQuery(id+"F0.wireOp",EDGE,"E268"),sQuery(id+"F0.wireOp",EDGE,"E269"),sQuery(id+"F0.wireOp",EDGE,"E270"),sQuery(id+"F0.wireOp",EDGE,"E271"),sQuery(id+"F0.wireOp",EDGE,"E272"),sQuery(id+"F0.wireOp",EDGE,"E273"),sQuery(id+"F0.wireOp",EDGE,"E274"),sQuery(id+"F0.wireOp",EDGE,"E275"),sQuery(id+"F0.wireOp",EDGE,"E276"),sQuery(id+"F0.wireOp",EDGE,"E277"),sQuery(id+"F0.wireOp",EDGE,"E278"),sQuery(id+"F0.wireOp",EDGE,"E279"),sQuery(id+"F0.wireOp",EDGE,"E280"),sQuery(id+"F0.wireOp",EDGE,"E281"),sQuery(id+"F0.wireOp",EDGE,"E282"),sQuery(id+"F0.wireOp",EDGE,"E283"),sQuery(id+"F0.wireOp",EDGE,"E284"),sQuery(id+"F0.wireOp",EDGE,"E285"),sQuery(id+"F0.wireOp",EDGE,"E286"),sQuery(id+"F0.wireOp",EDGE,"E287"),sQuery(id+"F0.wireOp",EDGE,"E288"),sQuery(id+"F0.wireOp",EDGE,"E289"),sQuery(id+"F0.wireOp",EDGE,"E290"),sQuery(id+"F0.wireOp",EDGE,"E291"),sQuery(id+"F0.wireOp",EDGE,"E292"),sQuery(id+"F0.wireOp",EDGE,"E293"),sQuery(id+"F0.wireOp",EDGE,"E294"),sQuery(id+"F0.wireOp",EDGE,"E295"),sQuery(id+"F0.wireOp",EDGE,"E296"),sQuery(id+"F0.wireOp",EDGE,"E297"),sQuery(id+"F0.wireOp",EDGE,"E298"),sQuery(id+"F0.wireOp",EDGE,"E299"),sQuery(id+"F0.wireOp",EDGE,"E300"),sQuery(id+"F0.wireOp",EDGE,"E301"),sQuery(id+"F0.wireOp",EDGE,"E302"),sQuery(id+"F0.wireOp",EDGE,"E303"),sQuery(id+"F0.wireOp",EDGE,"E304"),sQuery(id+"F0.wireOp",EDGE,"E305"),sQuery(id+"F0.wireOp",EDGE,"E306"),sQuery(id+"F0.wireOp",EDGE,"E307"),sQuery(id+"F0.wireOp",EDGE,"E308"),sQuery(id+"F0.wireOp",EDGE,"E309"),sQuery(id+"F0.wireOp",EDGE,"E310"),sQuery(id+"F0.wireOp",EDGE,"E311"),sQuery(id+"F0.wireOp",EDGE,"E312"),sQuery(id+"F0.wireOp",EDGE,"E313"),sQuery(id+"F0.wireOp",EDGE,"E314"),sQuery(id+"F0.wireOp",EDGE,"E315"),sQuery(id+"F0.wireOp",EDGE,"E316"),sQuery(id+"F0.wireOp",EDGE,"E317"),sQuery(id+"F0.wireOp",EDGE,"E318"),sQuery(id+"F0.wireOp",EDGE,"E319"),sQuery(id+"F0.wireOp",EDGE,"E320"),sQuery(id+"F0.wireOp",EDGE,"E321"),sQuery(id+"F0.wireOp",EDGE,"E322"),sQuery(id+"F0.wireOp",EDGE,"E323"),sQuery(id+"F0.wireOp",EDGE,"E324"),sQuery(id+"F0.wireOp",EDGE,"E325"),sQuery(id+"F0.wireOp",EDGE,"E326"),sQuery(id+"F0.wireOp",EDGE,"E327"),sQuery(id+"F0.wireOp",EDGE,"E328"),sQuery(id+"F0.wireOp",EDGE,"E329"),sQuery(id+"F0.wireOp",EDGE,"E330"),sQuery(id+"F0.wireOp",EDGE,"E331"),sQuery(id+"F0.wireOp",EDGE,"E332"),sQuery(id+"F0.wireOp",EDGE,"E333"),sQuery(id+"F0.wireOp",EDGE,"E334"),sQuery(id+"F0.wireOp",EDGE,"E335"),sQuery(id+"F0.wireOp",EDGE,"E336"),sQuery(id+"F0.wireOp",EDGE,"E337"),sQuery(id+"F0.wireOp",EDGE,"E338"),sQuery(id+"F0.wireOp",EDGE,"E339"),sQuery(id+"F0.wireOp",EDGE,"E340"),sQuery(id+"F0.wireOp",EDGE,"E341"),sQuery(id+"F0.wireOp",EDGE,"E342"),sQuery(id+"F0.wireOp",EDGE,"E343"),sQuery(id+"F0.wireOp",EDGE,"E344"),sQuery(id+"F0.wireOp",EDGE,"E345"),sQuery(id+"F0.wireOp",EDGE,"E346"),sQuery(id+"F0.wireOp",EDGE,"E347"),sQuery(id+"F0.wireOp",EDGE,"E348"),sQuery(id+"F0.wireOp",EDGE,"E349"),sQuery(id+"F0.wireOp",EDGE,"E350"),sQuery(id+"F0.wireOp",EDGE,"E351"),sQuery(id+"F0.wireOp",EDGE,"E352"),sQuery(id+"F0.wireOp",EDGE,"E353"),sQuery(id+"F0.wireOp",EDGE,"E354"),sQuery(id+"F0.wireOp",EDGE,"E355"),sQuery(id+"F0.wireOp",EDGE,"E356"),sQuery(id+"F0.wireOp",EDGE,"E357"),sQuery(id+"F0.wireOp",EDGE,"E358"),sQuery(id+"F0.wireOp",EDGE,"E359"),sQuery(id+"F0.wireOp",EDGE,"E360"),sQuery(id+"F0.wireOp",EDGE,"E361"),sQuery(id+"F0.wireOp",EDGE,"E362"),sQuery(id+"F0.wireOp",EDGE,"E363"),sQuery(id+"F0.wireOp",EDGE,"E364"),sQuery(id+"F0.wireOp",EDGE,"E365"),sQuery(id+"F0.wireOp",EDGE,"E366"),sQuery(id+"F0.wireOp",EDGE,"E367"),sQuery(id+"F0.wireOp",EDGE,"E368"),sQuery(id+"F0.wireOp",EDGE,"E369"),sQuery(id+"F0.wireOp",EDGE,"E370"),sQuery(id+"F0.wireOp",EDGE,"E371"),sQuery(id+"F0.wireOp",EDGE,"E372"),sQuery(id+"F0.wireOp",EDGE,"E373"),sQuery(id+"F0.wireOp",EDGE,"E374"),sQuery(id+"F0.wireOp",EDGE,"E375"),sQuery(id+"F0.wireOp",EDGE,"E376"),sQuery(id+"F0.wireOp",EDGE,"E377"),sQuery(id+"F0.wireOp",EDGE,"E378"),sQuery(id+"F0.wireOp",EDGE,"E379"),sQuery(id+"F0.wireOp",EDGE,"E380"),sQuery(id+"F0.wireOp",EDGE,"E381"),sQuery(id+"F0.wireOp",EDGE,"E382"),sQuery(id+"F0.wireOp",EDGE,"E383"),sQuery(id+"F0.wireOp",EDGE,"E384"),sQuery(id+"F0.wireOp",EDGE,"E385"),sQuery(id+"F0.wireOp",EDGE,"E386"),sQuery(id+"F0.wireOp",EDGE,"E387"),sQuery(id+"F0.wireOp",EDGE,"E388"),sQuery(id+"F0.wireOp",EDGE,"E389"),sQuery(id+"F0.wireOp",EDGE,"E390"),sQuery(id+"F0.wireOp",EDGE,"E391"),sQuery(id+"F0.wireOp",EDGE,"E392"),sQuery(id+"F0.wireOp",EDGE,"E393"),sQuery(id+"F0.wireOp",EDGE,"E394"),sQuery(id+"F0.wireOp",EDGE,"E395"),sQuery(id+"F0.wireOp",EDGE,"E396"),sQuery(id+"F0.wireOp",EDGE,"E397"),sQuery(id+"F0.wireOp",EDGE,"E398"),sQuery(id+"F0.wireOp",EDGE,"E399"),sQuery(id+"F0.wireOp",EDGE,"E400"),sQuery(id+"F0.wireOp",EDGE,"E401"),sQuery(id+"F0.wireOp",EDGE,"E402"),sQuery(id+"F0.wireOp",EDGE,"E403"),sQuery(id+"F0.wireOp",EDGE,"E404"),sQuery(id+"F0.wireOp",EDGE,"E405"),sQuery(id+"F0.wireOp",EDGE,"E406"),sQuery(id+"F0.wireOp",EDGE,"E407"),sQuery(id+"F0.wireOp",EDGE,"E408"),sQuery(id+"F0.wireOp",EDGE,"E409"),sQuery(id+"F0.wireOp",EDGE,"E410"),sQuery(id+"F0.wireOp",EDGE,"E411"),sQuery(id+"F0.wireOp",EDGE,"E412"),sQuery(id+"F0.wireOp",EDGE,"E413"),sQuery(id+"F0.wireOp",EDGE,"E414"),sQuery(id+"F0.wireOp",EDGE,"E415"),sQuery(id+"F0.wireOp",EDGE,"E416"),sQuery(id+"F0.wireOp",EDGE,"E417"),sQuery(id+"F0.wireOp",EDGE,"E418"),sQuery(id+"F0.wireOp",EDGE,"E419"),sQuery(id+"F0.wireOp",EDGE,"E420"),sQuery(id+"F0.wireOp",EDGE,"E421"),sQuery(id+"F0.wireOp",EDGE,"E422"),sQuery(id+"F0.wireOp",EDGE,"E423"),sQuery(id+"F0.wireOp",EDGE,"E424"),sQuery(id+"F0.wireOp",EDGE,"E425"),sQuery(id+"F0.wireOp",EDGE,"E426"),sQuery(id+"F0.wireOp",EDGE,"E427"),sQuery(id+"F0.wireOp",EDGE,"E428"),sQuery(id+"F0.wireOp",EDGE,"E429"),sQuery(id+"F0.wireOp",EDGE,"E430"),sQuery(id+"F0.wireOp",EDGE,"E431"),sQuery(id+"F0.wireOp",EDGE,"E432"),sQuery(id+"F0.wireOp",EDGE,"E433"),sQuery(id+"F0.wireOp",EDGE,"E434"),sQuery(id+"F0.wireOp",EDGE,"E435"),sQuery(id+"F0.wireOp",EDGE,"E436"),sQuery(id+"F0.wireOp",EDGE,"E437"),sQuery(id+"F0.wireOp",EDGE,"E438"),sQuery(id+"F0.wireOp",EDGE,"E439"),sQuery(id+"F0.wireOp",EDGE,"E440"),sQuery(id+"F0.wireOp",EDGE,"E441"),sQuery(id+"F0.wireOp",EDGE,"E442"),sQuery(id+"F0.wireOp",EDGE,"E443"),sQuery(id+"F0.wireOp",EDGE,"E444"),sQuery(id+"F0.wireOp",EDGE,"E445"),sQuery(id+"F0.wireOp",EDGE,"E446"),sQuery(id+"F0.wireOp",EDGE,"E447"),sQuery(id+"F0.wireOp",EDGE,"E448"),sQuery(id+"F0.wireOp",EDGE,"E449"),sQuery(id+"F0.wireOp",EDGE,"E450"),sQuery(id+"F0.wireOp",EDGE,"E451"),sQuery(id+"F0.wireOp",EDGE,"E452"),sQuery(id+"F0.wireOp",EDGE,"E453"),sQuery(id+"F0.wireOp",EDGE,"E454"),sQuery(id+"F0.wireOp",EDGE,"E455"),sQuery(id+"F0.wireOp",EDGE,"E456"),sQuery(id+"F0.wireOp",EDGE,"E457"),sQuery(id+"F0.wireOp",EDGE,"E458"),sQuery(id+"F0.wireOp",EDGE,"E459"),sQuery(id+"F0.wireOp",EDGE,"E460"),sQuery(id+"F0.wireOp",EDGE,"E461"),sQuery(id+"F0.wireOp",EDGE,"E462"),sQuery(id+"F0.wireOp",EDGE,"E463"),sQuery(id+"F0.wireOp",EDGE,"E464"),sQuery(id+"F0.wireOp",EDGE,"E465"),sQuery(id+"F0.wireOp",EDGE,"E466"),sQuery(id+"F0.wireOp",EDGE,"E467"),sQuery(id+"F0.wireOp",EDGE,"E468"),sQuery(id+"F0.wireOp",EDGE,"E469"),sQuery(id+"F0.wireOp",EDGE,"E470"),sQuery(id+"F0.wireOp",EDGE,"E471"),sQuery(id+"F0.wireOp",EDGE,"E472"),sQuery(id+"F0.wireOp",EDGE,"E473"),sQuery(id+"F0.wireOp",EDGE,"E474"),sQuery(id+"F0.wireOp",EDGE,"E475"),sQuery(id+"F0.wireOp",EDGE,"E476"),sQuery(id+"F0.wireOp",EDGE,"E477"),sQuery(id+"F0.wireOp",EDGE,"E478"),sQuery(id+"F0.wireOp",EDGE,"E479"),sQuery(id+"F0.wireOp",EDGE,"E480"),sQuery(id+"F0.wireOp",EDGE,"E481"),sQuery(id+"F0.wireOp",EDGE,"E482"),sQuery(id+"F0.wireOp",EDGE,"E483"),sQuery(id+"F0.wireOp",EDGE,"E484"),sQuery(id+"F0.wireOp",EDGE,"E485"),sQuery(id+"F0.wireOp",EDGE,"E486"),sQuery(id+"F0.wireOp",EDGE,"E487"),sQuery(id+"F0.wireOp",EDGE,"E488"),sQuery(id+"F0.wireOp",EDGE,"E489"),sQuery(id+"F0.wireOp",EDGE,"E490"),sQuery(id+"F0.wireOp",EDGE,"E491"),sQuery(id+"F0.wireOp",EDGE,"E492"),sQuery(id+"F0.wireOp",EDGE,"E493"),sQuery(id+"F0.wireOp",EDGE,"E494"),sQuery(id+"F0.wireOp",EDGE,"E495"),sQuery(id+"F0.wireOp",EDGE,"E496"),sQuery(id+"F0.wireOp",EDGE,"E497"),sQuery(id+"F0.wireOp",EDGE,"E498"),sQuery(id+"F0.wireOp",EDGE,"E499"),sQuery(id+"F0.wireOp",EDGE,"E500"),sQuery(id+"F0.wireOp",EDGE,"E501"),sQuery(id+"F0.wireOp",EDGE,"E502"),sQuery(id+"F0.wireOp",EDGE,"E503"),sQuery(id+"F0.wireOp",EDGE,"E504"),sQuery(id+"F0.wireOp",EDGE,"E505"),sQuery(id+"F0.wireOp",EDGE,"E506"),sQuery(id+"F0.wireOp",EDGE,"E507"),sQuery(id+"F0.wireOp",EDGE,"E508"),sQuery(id+"F0.wireOp",EDGE,"E509"),sQuery(id+"F0.wireOp",EDGE,"E510"),sQuery(id+"F0.wireOp",EDGE,"E511"),sQuery(id+"F0.wireOp",EDGE,"E512"),sQuery(id+"F0.wireOp",EDGE,"E513"),sQuery(id+"F0.wireOp",EDGE,"E514"),sQuery(id+"F0.wireOp",EDGE,"E515"),sQuery(id+"F0.wireOp",EDGE,"E516"),sQuery(id+"F0.wireOp",EDGE,"E517"),sQuery(id+"F0.wireOp",EDGE,"E518"),sQuery(id+"F0.wireOp",EDGE,"E519"),sQuery(id+"F0.wireOp",EDGE,"E520"),sQuery(id+"F0.wireOp",EDGE,"E521"),sQuery(id+"F0.wireOp",EDGE,"E522"),sQuery(id+"F0.wireOp",EDGE,"E523"),sQuery(id+"F0.wireOp",EDGE,"E524"),sQuery(id+"F0.wireOp",EDGE,"E525"),sQuery(id+"F0.wireOp",EDGE,"E526"),sQuery(id+"F0.wireOp",EDGE,"E527"),sQuery(id+"F0.wireOp",EDGE,"E528"),sQuery(id+"F0.wireOp",EDGE,"E529"),sQuery(id+"F0.wireOp",EDGE,"E530"),sQuery(id+"F0.wireOp",EDGE,"E531"),sQuery(id+"F0.wireOp",EDGE,"E532"),sQuery(id+"F0.wireOp",EDGE,"E533"),sQuery(id+"F0.wireOp",EDGE,"E534"),sQuery(id+"F0.wireOp",EDGE,"E535"),sQuery(id+"F0.wireOp",EDGE,"E536"),sQuery(id+"F0.wireOp",EDGE,"E537"),sQuery(id+"F0.wireOp",EDGE,"E538"),sQuery(id+"F0.wireOp",EDGE,"E539"),sQuery(id+"F0.wireOp",EDGE,"E540"),sQuery(id+"F0.wireOp",EDGE,"E541"),sQuery(id+"F0.wireOp",EDGE,"E542"),sQuery(id+"F0.wireOp",EDGE,"E543"),sQuery(id+"F0.wireOp",EDGE,"E544"),sQuery(id+"F0.wireOp",EDGE,"E545"),sQuery(id+"F0.wireOp",EDGE,"E546"),sQuery(id+"F0.wireOp",EDGE,"E547"),sQuery(id+"F0.wireOp",EDGE,"E548"),sQuery(id+"F0.wireOp",EDGE,"E549"),sQuery(id+"F0.wireOp",EDGE,"E550"),sQuery(id+"F0.wireOp",EDGE,"E551"),sQuery(id+"F0.wireOp",EDGE,"E552"),sQuery(id+"F0.wireOp",EDGE,"E553"),sQuery(id+"F0.wireOp",EDGE,"E554"),sQuery(id+"F0.wireOp",EDGE,"E555"),sQuery(id+"F0.wireOp",EDGE,"E556"),sQuery(id+"F0.wireOp",EDGE,"E557"),sQuery(id+"F0.wireOp",EDGE,"E558"),sQuery(id+"F0.wireOp",EDGE,"E559"),sQuery(id+"F0.wireOp",EDGE,"E560"),sQuery(id+"F0.wireOp",EDGE,"E561"),sQuery(id+"F0.wireOp",EDGE,"E562"),sQuery(id+"F0.wireOp",EDGE,"E563"),sQuery(id+"F0.wireOp",EDGE,"E564"),sQuery(id+"F0.wireOp",EDGE,"E565"),sQuery(id+"F0.wireOp",EDGE,"E566"),sQuery(id+"F0.wireOp",EDGE,"E567"),sQuery(id+"F0.wireOp",EDGE,"E568"),sQuery(id+"F0.wireOp",EDGE,"E569"),sQuery(id+"F0.wireOp",EDGE,"0a7d94a7-0c48-4280-a40c-ca015d1273c1"),sQuery(id+"F0.wireOp",EDGE,"6faaf318-2b60-4bcc-8c42-29dbb8ba8157"),sQuery(id+"F0.wireOp",EDGE,"6fab337f-4268-44d8-9b83-a8af3216684d"),sQuery(id+"F0.wireOp",EDGE,"ae5d5c7b-5ab5-415f-8ac6-d32b1c8cfa1f"),sQuery(id+"F0.wireOp",EDGE,"e4c0af21-179e-4c74-a26c-390a930c27a0"),sQuery(id+"F0.wireOp",EDGE,"b2a82f03-3352-433a-a6ce-47b4fc5c4f7d"),sQuery(id+"F0.wireOp",EDGE,"401c6160-c13a-4bb2-8453-ae57bc2561d0"),sQuery(id+"F0.wireOp",EDGE,"b9c8c5a8-604d-4089-bc0e-c269181b05a1"),sQuery(id+"F0.wireOp",EDGE,"d13bc520-7fdf-44d4-befa-9bb74a98d9ac"),sQuery(id+"F0.wireOp",EDGE,"0c6945d6-83c7-41a2-bbe0-9151480165d1"),sQuery(id+"F0.wireOp",EDGE,"c2e5544b-6f1d-4b5a-9d7f-a316d665aab7"),sQuery(id+"F0.wireOp",EDGE,"3f8cc766-92eb-470c-8976-8292643858b8"),sQuery(id+"F0.wireOp",EDGE,"e2c96489-0516-49be-949a-232fc3b08c6e"),sQuery(id+"F0.wireOp",EDGE,"dc1fdd5e-f3e1-478f-855b-0954b7da4f3a"),sQuery(id+"F0.wireOp",EDGE,"206881de-fbc1-44f4-a58e-f01c1af56eda"),sQuery(id+"F0.wireOp",EDGE,"da4ecaad-c66d-41b2-a35d-ee2c3f2e975c"),sQuery(id+"F0.wireOp",EDGE,"c0e9e4f0-8bc3-4eed-8bdd-ec4dc1827391"),sQuery(id+"F0.wireOp",EDGE,"3fcb0153-1e5b-4ec1-8e87-eebd5594ab18"),sQuery(id+"F0.wireOp",EDGE,"fa9ef4b5-4ad0-46e5-87e4-16d7e9957144"),sQuery(id+"F0.wireOp",EDGE,"cfb04778-b9ee-424c-aa58-1acd9e0b25d3"),sQuery(id+"F0.wireOp",EDGE,"ac5241aa-82b5-483c-aedd-2e68e624b3d0"),sQuery(id+"F0.wireOp",EDGE,"c0d771a4-9243-4f4a-91ba-28cc73d4316c"),sQuery(id+"F0.wireOp",EDGE,"e2694bdb-ffb1-4603-8b5b-c3e610f4d87f"),sQuery(id+"F0.wireOp",EDGE,"4b9f8550-4284-4f4b-810e-1e288d83531a"),sQuery(id+"F0.wireOp",EDGE,"df2ecc50-d025-48d4-b418-12de0cec21e9"),sQuery(id+"F0.wireOp",EDGE,"40ff5135-8e85-4843-a980-f3de56f4e5ef"),sQuery(id+"F0.wireOp",EDGE,"098b022f-6fc7-4080-8c3d-07ac9e931079"),sQuery(id+"F0.wireOp",EDGE,"56bb8ea8-df13-41fc-a47b-d443a017a7d1"),sQuery(id+"F0.wireOp",EDGE,"d371b615-971a-4aa0-971b-998f5da94f7b"),sQuery(id+"F0.wireOp",EDGE,"5c2c628b-7d24-44e3-b1c6-5ca418c1f165")])]});
            var Q1;
            Q1=qCreatedBy(makeId("Origin.pointOp"),VERTEX);
            transform(context, id + "F2", {"entities" : qUnion([Q0]), "transformType" : TransformType.SCALE_UNIFORMLY, "scale" : 0.02, "scalePoint" : qUnion([Q1]), "makeCopy" : false});
        }
        {
            var Q0;
            Q0=makeQuery(id+"F1.opExtrude","CAP_FACE",FACE,{"disambiguationData":[OSD([sQuery(id+"F0.wireOp",EDGE,"E0"),sQuery(id+"F0.wireOp",EDGE,"E1"),sQuery(id+"F0.wireOp",EDGE,"E2"),sQuery(id+"F0.wireOp",EDGE,"E3"),sQuery(id+"F0.wireOp",EDGE,"E4"),sQuery(id+"F0.wireOp",EDGE,"E5"),sQuery(id+"F0.wireOp",EDGE,"E6"),sQuery(id+"F0.wireOp",EDGE,"E7"),sQuery(id+"F0.wireOp",EDGE,"E8"),sQuery(id+"F0.wireOp",EDGE,"E9"),sQuery(id+"F0.wireOp",EDGE,"E10"),sQuery(id+"F0.wireOp",EDGE,"E11"),sQuery(id+"F0.wireOp",EDGE,"E12"),sQuery(id+"F0.wireOp",EDGE,"E13"),sQuery(id+"F0.wireOp",EDGE,"E14"),sQuery(id+"F0.wireOp",EDGE,"E15"),sQuery(id+"F0.wireOp",EDGE,"E16"),sQuery(id+"F0.wireOp",EDGE,"E17"),sQuery(id+"F0.wireOp",EDGE,"E18"),sQuery(id+"F0.wireOp",EDGE,"E19"),sQuery(id+"F0.wireOp",EDGE,"E20"),sQuery(id+"F0.wireOp",EDGE,"E21"),sQuery(id+"F0.wireOp",EDGE,"E22"),sQuery(id+"F0.wireOp",EDGE,"E23"),sQuery(id+"F0.wireOp",EDGE,"E24"),sQuery(id+"F0.wireOp",EDGE,"E25"),sQuery(id+"F0.wireOp",EDGE,"E26"),sQuery(id+"F0.wireOp",EDGE,"E27"),sQuery(id+"F0.wireOp",EDGE,"E28"),sQuery(id+"F0.wireOp",EDGE,"E29"),sQuery(id+"F0.wireOp",EDGE,"E30"),sQuery(id+"F0.wireOp",EDGE,"E31"),sQuery(id+"F0.wireOp",EDGE,"E32"),sQuery(id+"F0.wireOp",EDGE,"E33"),sQuery(id+"F0.wireOp",EDGE,"E34"),sQuery(id+"F0.wireOp",EDGE,"E35"),sQuery(id+"F0.wireOp",EDGE,"E36"),sQuery(id+"F0.wireOp",EDGE,"E37"),sQuery(id+"F0.wireOp",EDGE,"E38"),sQuery(id+"F0.wireOp",EDGE,"E39"),sQuery(id+"F0.wireOp",EDGE,"E40"),sQuery(id+"F0.wireOp",EDGE,"E41"),sQuery(id+"F0.wireOp",EDGE,"E42"),sQuery(id+"F0.wireOp",EDGE,"E43"),sQuery(id+"F0.wireOp",EDGE,"E44"),sQuery(id+"F0.wireOp",EDGE,"E45"),sQuery(id+"F0.wireOp",EDGE,"E46"),sQuery(id+"F0.wireOp",EDGE,"E47"),sQuery(id+"F0.wireOp",EDGE,"E48"),sQuery(id+"F0.wireOp",EDGE,"E49"),sQuery(id+"F0.wireOp",EDGE,"E50"),sQuery(id+"F0.wireOp",EDGE,"E51"),sQuery(id+"F0.wireOp",EDGE,"E52"),sQuery(id+"F0.wireOp",EDGE,"E53"),sQuery(id+"F0.wireOp",EDGE,"E54"),sQuery(id+"F0.wireOp",EDGE,"E55"),sQuery(id+"F0.wireOp",EDGE,"E56"),sQuery(id+"F0.wireOp",EDGE,"E57"),sQuery(id+"F0.wireOp",EDGE,"E58"),sQuery(id+"F0.wireOp",EDGE,"E59"),sQuery(id+"F0.wireOp",EDGE,"E60"),sQuery(id+"F0.wireOp",EDGE,"E61"),sQuery(id+"F0.wireOp",EDGE,"E62"),sQuery(id+"F0.wireOp",EDGE,"E63"),sQuery(id+"F0.wireOp",EDGE,"E64"),sQuery(id+"F0.wireOp",EDGE,"E65"),sQuery(id+"F0.wireOp",EDGE,"E66"),sQuery(id+"F0.wireOp",EDGE,"E67"),sQuery(id+"F0.wireOp",EDGE,"E68"),sQuery(id+"F0.wireOp",EDGE,"E69"),sQuery(id+"F0.wireOp",EDGE,"E70"),sQuery(id+"F0.wireOp",EDGE,"E71"),sQuery(id+"F0.wireOp",EDGE,"E72"),sQuery(id+"F0.wireOp",EDGE,"E73"),sQuery(id+"F0.wireOp",EDGE,"E74"),sQuery(id+"F0.wireOp",EDGE,"E75"),sQuery(id+"F0.wireOp",EDGE,"E76"),sQuery(id+"F0.wireOp",EDGE,"E77"),sQuery(id+"F0.wireOp",EDGE,"E78"),sQuery(id+"F0.wireOp",EDGE,"E79"),sQuery(id+"F0.wireOp",EDGE,"E80"),sQuery(id+"F0.wireOp",EDGE,"E81"),sQuery(id+"F0.wireOp",EDGE,"E82"),sQuery(id+"F0.wireOp",EDGE,"E83"),sQuery(id+"F0.wireOp",EDGE,"E84"),sQuery(id+"F0.wireOp",EDGE,"E85"),sQuery(id+"F0.wireOp",EDGE,"E86"),sQuery(id+"F0.wireOp",EDGE,"E87"),sQuery(id+"F0.wireOp",EDGE,"E88"),sQuery(id+"F0.wireOp",EDGE,"E89"),sQuery(id+"F0.wireOp",EDGE,"E90"),sQuery(id+"F0.wireOp",EDGE,"E91"),sQuery(id+"F0.wireOp",EDGE,"E92"),sQuery(id+"F0.wireOp",EDGE,"E93"),sQuery(id+"F0.wireOp",EDGE,"E94"),sQuery(id+"F0.wireOp",EDGE,"E95"),sQuery(id+"F0.wireOp",EDGE,"E96"),sQuery(id+"F0.wireOp",EDGE,"E97"),sQuery(id+"F0.wireOp",EDGE,"E98"),sQuery(id+"F0.wireOp",EDGE,"E99"),sQuery(id+"F0.wireOp",EDGE,"E100"),sQuery(id+"F0.wireOp",EDGE,"E101"),sQuery(id+"F0.wireOp",EDGE,"E102"),sQuery(id+"F0.wireOp",EDGE,"E103"),sQuery(id+"F0.wireOp",EDGE,"E104"),sQuery(id+"F0.wireOp",EDGE,"E105"),sQuery(id+"F0.wireOp",EDGE,"E106"),sQuery(id+"F0.wireOp",EDGE,"E107"),sQuery(id+"F0.wireOp",EDGE,"E108"),sQuery(id+"F0.wireOp",EDGE,"E109"),sQuery(id+"F0.wireOp",EDGE,"E110"),sQuery(id+"F0.wireOp",EDGE,"E111"),sQuery(id+"F0.wireOp",EDGE,"E112"),sQuery(id+"F0.wireOp",EDGE,"E113"),sQuery(id+"F0.wireOp",EDGE,"E114"),sQuery(id+"F0.wireOp",EDGE,"E115"),sQuery(id+"F0.wireOp",EDGE,"E116"),sQuery(id+"F0.wireOp",EDGE,"E117"),sQuery(id+"F0.wireOp",EDGE,"E118"),sQuery(id+"F0.wireOp",EDGE,"E119"),sQuery(id+"F0.wireOp",EDGE,"E120"),sQuery(id+"F0.wireOp",EDGE,"E121"),sQuery(id+"F0.wireOp",EDGE,"E122"),sQuery(id+"F0.wireOp",EDGE,"E123"),sQuery(id+"F0.wireOp",EDGE,"E124"),sQuery(id+"F0.wireOp",EDGE,"E125"),sQuery(id+"F0.wireOp",EDGE,"E126"),sQuery(id+"F0.wireOp",EDGE,"E127"),sQuery(id+"F0.wireOp",EDGE,"E128"),sQuery(id+"F0.wireOp",EDGE,"E129"),sQuery(id+"F0.wireOp",EDGE,"E130"),sQuery(id+"F0.wireOp",EDGE,"E131"),sQuery(id+"F0.wireOp",EDGE,"E132"),sQuery(id+"F0.wireOp",EDGE,"E133"),sQuery(id+"F0.wireOp",EDGE,"E134"),sQuery(id+"F0.wireOp",EDGE,"E135"),sQuery(id+"F0.wireOp",EDGE,"E136"),sQuery(id+"F0.wireOp",EDGE,"E137"),sQuery(id+"F0.wireOp",EDGE,"E138"),sQuery(id+"F0.wireOp",EDGE,"E139"),sQuery(id+"F0.wireOp",EDGE,"E140"),sQuery(id+"F0.wireOp",EDGE,"E141"),sQuery(id+"F0.wireOp",EDGE,"E142"),sQuery(id+"F0.wireOp",EDGE,"E143"),sQuery(id+"F0.wireOp",EDGE,"E144"),sQuery(id+"F0.wireOp",EDGE,"E145"),sQuery(id+"F0.wireOp",EDGE,"E146"),sQuery(id+"F0.wireOp",EDGE,"E147"),sQuery(id+"F0.wireOp",EDGE,"E148"),sQuery(id+"F0.wireOp",EDGE,"E149"),sQuery(id+"F0.wireOp",EDGE,"E150"),sQuery(id+"F0.wireOp",EDGE,"E151"),sQuery(id+"F0.wireOp",EDGE,"E152"),sQuery(id+"F0.wireOp",EDGE,"E153"),sQuery(id+"F0.wireOp",EDGE,"E154"),sQuery(id+"F0.wireOp",EDGE,"E155"),sQuery(id+"F0.wireOp",EDGE,"E156"),sQuery(id+"F0.wireOp",EDGE,"E157"),sQuery(id+"F0.wireOp",EDGE,"E158"),sQuery(id+"F0.wireOp",EDGE,"E159"),sQuery(id+"F0.wireOp",EDGE,"E160"),sQuery(id+"F0.wireOp",EDGE,"E161"),sQuery(id+"F0.wireOp",EDGE,"E162"),sQuery(id+"F0.wireOp",EDGE,"E163"),sQuery(id+"F0.wireOp",EDGE,"E164"),sQuery(id+"F0.wireOp",EDGE,"E165"),sQuery(id+"F0.wireOp",EDGE,"E166"),sQuery(id+"F0.wireOp",EDGE,"E167"),sQuery(id+"F0.wireOp",EDGE,"E168"),sQuery(id+"F0.wireOp",EDGE,"E169"),sQuery(id+"F0.wireOp",EDGE,"E170"),sQuery(id+"F0.wireOp",EDGE,"E171"),sQuery(id+"F0.wireOp",EDGE,"E172"),sQuery(id+"F0.wireOp",EDGE,"E173"),sQuery(id+"F0.wireOp",EDGE,"E174"),sQuery(id+"F0.wireOp",EDGE,"E175"),sQuery(id+"F0.wireOp",EDGE,"E176"),sQuery(id+"F0.wireOp",EDGE,"E177"),sQuery(id+"F0.wireOp",EDGE,"E178"),sQuery(id+"F0.wireOp",EDGE,"E179"),sQuery(id+"F0.wireOp",EDGE,"E180"),sQuery(id+"F0.wireOp",EDGE,"E181"),sQuery(id+"F0.wireOp",EDGE,"E182"),sQuery(id+"F0.wireOp",EDGE,"E183"),sQuery(id+"F0.wireOp",EDGE,"E184"),sQuery(id+"F0.wireOp",EDGE,"E185"),sQuery(id+"F0.wireOp",EDGE,"E186"),sQuery(id+"F0.wireOp",EDGE,"E187"),sQuery(id+"F0.wireOp",EDGE,"E188"),sQuery(id+"F0.wireOp",EDGE,"E189"),sQuery(id+"F0.wireOp",EDGE,"E190"),sQuery(id+"F0.wireOp",EDGE,"E191"),sQuery(id+"F0.wireOp",EDGE,"E192"),sQuery(id+"F0.wireOp",EDGE,"E193"),sQuery(id+"F0.wireOp",EDGE,"E194"),sQuery(id+"F0.wireOp",EDGE,"E195"),sQuery(id+"F0.wireOp",EDGE,"E196"),sQuery(id+"F0.wireOp",EDGE,"E197"),sQuery(id+"F0.wireOp",EDGE,"E198"),sQuery(id+"F0.wireOp",EDGE,"E199"),sQuery(id+"F0.wireOp",EDGE,"E200"),sQuery(id+"F0.wireOp",EDGE,"E201"),sQuery(id+"F0.wireOp",EDGE,"E202"),sQuery(id+"F0.wireOp",EDGE,"E203"),sQuery(id+"F0.wireOp",EDGE,"E204"),sQuery(id+"F0.wireOp",EDGE,"E205"),sQuery(id+"F0.wireOp",EDGE,"E206"),sQuery(id+"F0.wireOp",EDGE,"E207"),sQuery(id+"F0.wireOp",EDGE,"E208"),sQuery(id+"F0.wireOp",EDGE,"E209"),sQuery(id+"F0.wireOp",EDGE,"E210"),sQuery(id+"F0.wireOp",EDGE,"E211"),sQuery(id+"F0.wireOp",EDGE,"E212"),sQuery(id+"F0.wireOp",EDGE,"E213"),sQuery(id+"F0.wireOp",EDGE,"E214"),sQuery(id+"F0.wireOp",EDGE,"E215"),sQuery(id+"F0.wireOp",EDGE,"E216"),sQuery(id+"F0.wireOp",EDGE,"E217"),sQuery(id+"F0.wireOp",EDGE,"E218"),sQuery(id+"F0.wireOp",EDGE,"E219"),sQuery(id+"F0.wireOp",EDGE,"E220"),sQuery(id+"F0.wireOp",EDGE,"E221"),sQuery(id+"F0.wireOp",EDGE,"E222"),sQuery(id+"F0.wireOp",EDGE,"E223"),sQuery(id+"F0.wireOp",EDGE,"E224"),sQuery(id+"F0.wireOp",EDGE,"E225"),sQuery(id+"F0.wireOp",EDGE,"E226"),sQuery(id+"F0.wireOp",EDGE,"E227"),sQuery(id+"F0.wireOp",EDGE,"E228"),sQuery(id+"F0.wireOp",EDGE,"E229"),sQuery(id+"F0.wireOp",EDGE,"E230"),sQuery(id+"F0.wireOp",EDGE,"E231"),sQuery(id+"F0.wireOp",EDGE,"E232"),sQuery(id+"F0.wireOp",EDGE,"E233"),sQuery(id+"F0.wireOp",EDGE,"E234"),sQuery(id+"F0.wireOp",EDGE,"E235"),sQuery(id+"F0.wireOp",EDGE,"E236"),sQuery(id+"F0.wireOp",EDGE,"E237"),sQuery(id+"F0.wireOp",EDGE,"E238"),sQuery(id+"F0.wireOp",EDGE,"E239"),sQuery(id+"F0.wireOp",EDGE,"E240"),sQuery(id+"F0.wireOp",EDGE,"E241"),sQuery(id+"F0.wireOp",EDGE,"E242"),sQuery(id+"F0.wireOp",EDGE,"E243"),sQuery(id+"F0.wireOp",EDGE,"E244"),sQuery(id+"F0.wireOp",EDGE,"E245"),sQuery(id+"F0.wireOp",EDGE,"E246"),sQuery(id+"F0.wireOp",EDGE,"E247"),sQuery(id+"F0.wireOp",EDGE,"E248"),sQuery(id+"F0.wireOp",EDGE,"E249"),sQuery(id+"F0.wireOp",EDGE,"E250"),sQuery(id+"F0.wireOp",EDGE,"E251"),sQuery(id+"F0.wireOp",EDGE,"E252"),sQuery(id+"F0.wireOp",EDGE,"E253"),sQuery(id+"F0.wireOp",EDGE,"E254"),sQuery(id+"F0.wireOp",EDGE,"E255"),sQuery(id+"F0.wireOp",EDGE,"E256"),sQuery(id+"F0.wireOp",EDGE,"E257"),sQuery(id+"F0.wireOp",EDGE,"E258"),sQuery(id+"F0.wireOp",EDGE,"E259"),sQuery(id+"F0.wireOp",EDGE,"E260"),sQuery(id+"F0.wireOp",EDGE,"E261"),sQuery(id+"F0.wireOp",EDGE,"E262"),sQuery(id+"F0.wireOp",EDGE,"E263"),sQuery(id+"F0.wireOp",EDGE,"E264"),sQuery(id+"F0.wireOp",EDGE,"E265"),sQuery(id+"F0.wireOp",EDGE,"E266"),sQuery(id+"F0.wireOp",EDGE,"E267"),sQuery(id+"F0.wireOp",EDGE,"E268"),sQuery(id+"F0.wireOp",EDGE,"E269"),sQuery(id+"F0.wireOp",EDGE,"E270"),sQuery(id+"F0.wireOp",EDGE,"E271"),sQuery(id+"F0.wireOp",EDGE,"E272"),sQuery(id+"F0.wireOp",EDGE,"E273"),sQuery(id+"F0.wireOp",EDGE,"E274"),sQuery(id+"F0.wireOp",EDGE,"E275"),sQuery(id+"F0.wireOp",EDGE,"E276"),sQuery(id+"F0.wireOp",EDGE,"E277"),sQuery(id+"F0.wireOp",EDGE,"E278"),sQuery(id+"F0.wireOp",EDGE,"E279"),sQuery(id+"F0.wireOp",EDGE,"E280"),sQuery(id+"F0.wireOp",EDGE,"E281"),sQuery(id+"F0.wireOp",EDGE,"E282"),sQuery(id+"F0.wireOp",EDGE,"E283"),sQuery(id+"F0.wireOp",EDGE,"E284"),sQuery(id+"F0.wireOp",EDGE,"E285"),sQuery(id+"F0.wireOp",EDGE,"E286"),sQuery(id+"F0.wireOp",EDGE,"E287"),sQuery(id+"F0.wireOp",EDGE,"E288"),sQuery(id+"F0.wireOp",EDGE,"E289"),sQuery(id+"F0.wireOp",EDGE,"E290"),sQuery(id+"F0.wireOp",EDGE,"E291"),sQuery(id+"F0.wireOp",EDGE,"E292"),sQuery(id+"F0.wireOp",EDGE,"E293"),sQuery(id+"F0.wireOp",EDGE,"E294"),sQuery(id+"F0.wireOp",EDGE,"E295"),sQuery(id+"F0.wireOp",EDGE,"E296"),sQuery(id+"F0.wireOp",EDGE,"E297"),sQuery(id+"F0.wireOp",EDGE,"E298"),sQuery(id+"F0.wireOp",EDGE,"E299"),sQuery(id+"F0.wireOp",EDGE,"E300"),sQuery(id+"F0.wireOp",EDGE,"E301"),sQuery(id+"F0.wireOp",EDGE,"E302"),sQuery(id+"F0.wireOp",EDGE,"E303"),sQuery(id+"F0.wireOp",EDGE,"E304"),sQuery(id+"F0.wireOp",EDGE,"E305"),sQuery(id+"F0.wireOp",EDGE,"E306"),sQuery(id+"F0.wireOp",EDGE,"E307"),sQuery(id+"F0.wireOp",EDGE,"E308"),sQuery(id+"F0.wireOp",EDGE,"E309"),sQuery(id+"F0.wireOp",EDGE,"E310"),sQuery(id+"F0.wireOp",EDGE,"E311"),sQuery(id+"F0.wireOp",EDGE,"E312"),sQuery(id+"F0.wireOp",EDGE,"E313"),sQuery(id+"F0.wireOp",EDGE,"E314"),sQuery(id+"F0.wireOp",EDGE,"E315"),sQuery(id+"F0.wireOp",EDGE,"E316"),sQuery(id+"F0.wireOp",EDGE,"E317"),sQuery(id+"F0.wireOp",EDGE,"E318"),sQuery(id+"F0.wireOp",EDGE,"E319"),sQuery(id+"F0.wireOp",EDGE,"E320"),sQuery(id+"F0.wireOp",EDGE,"E321"),sQuery(id+"F0.wireOp",EDGE,"E322"),sQuery(id+"F0.wireOp",EDGE,"E323"),sQuery(id+"F0.wireOp",EDGE,"E324"),sQuery(id+"F0.wireOp",EDGE,"E325"),sQuery(id+"F0.wireOp",EDGE,"E326"),sQuery(id+"F0.wireOp",EDGE,"E327"),sQuery(id+"F0.wireOp",EDGE,"E328"),sQuery(id+"F0.wireOp",EDGE,"E329"),sQuery(id+"F0.wireOp",EDGE,"E330"),sQuery(id+"F0.wireOp",EDGE,"E331"),sQuery(id+"F0.wireOp",EDGE,"E332"),sQuery(id+"F0.wireOp",EDGE,"E333"),sQuery(id+"F0.wireOp",EDGE,"E334"),sQuery(id+"F0.wireOp",EDGE,"E335"),sQuery(id+"F0.wireOp",EDGE,"E336"),sQuery(id+"F0.wireOp",EDGE,"E337"),sQuery(id+"F0.wireOp",EDGE,"E338"),sQuery(id+"F0.wireOp",EDGE,"E339"),sQuery(id+"F0.wireOp",EDGE,"E340"),sQuery(id+"F0.wireOp",EDGE,"E341"),sQuery(id+"F0.wireOp",EDGE,"E342"),sQuery(id+"F0.wireOp",EDGE,"E343"),sQuery(id+"F0.wireOp",EDGE,"E344"),sQuery(id+"F0.wireOp",EDGE,"E345"),sQuery(id+"F0.wireOp",EDGE,"E346"),sQuery(id+"F0.wireOp",EDGE,"E347"),sQuery(id+"F0.wireOp",EDGE,"E348"),sQuery(id+"F0.wireOp",EDGE,"E349"),sQuery(id+"F0.wireOp",EDGE,"E350"),sQuery(id+"F0.wireOp",EDGE,"E351"),sQuery(id+"F0.wireOp",EDGE,"E352"),sQuery(id+"F0.wireOp",EDGE,"E353"),sQuery(id+"F0.wireOp",EDGE,"E354"),sQuery(id+"F0.wireOp",EDGE,"E355"),sQuery(id+"F0.wireOp",EDGE,"E356"),sQuery(id+"F0.wireOp",EDGE,"E357"),sQuery(id+"F0.wireOp",EDGE,"E358"),sQuery(id+"F0.wireOp",EDGE,"E359"),sQuery(id+"F0.wireOp",EDGE,"E360"),sQuery(id+"F0.wireOp",EDGE,"E361"),sQuery(id+"F0.wireOp",EDGE,"E362"),sQuery(id+"F0.wireOp",EDGE,"E363"),sQuery(id+"F0.wireOp",EDGE,"E364"),sQuery(id+"F0.wireOp",EDGE,"E365"),sQuery(id+"F0.wireOp",EDGE,"E366"),sQuery(id+"F0.wireOp",EDGE,"E367"),sQuery(id+"F0.wireOp",EDGE,"E368"),sQuery(id+"F0.wireOp",EDGE,"E369"),sQuery(id+"F0.wireOp",EDGE,"E370"),sQuery(id+"F0.wireOp",EDGE,"E371"),sQuery(id+"F0.wireOp",EDGE,"E372"),sQuery(id+"F0.wireOp",EDGE,"E373"),sQuery(id+"F0.wireOp",EDGE,"E374"),sQuery(id+"F0.wireOp",EDGE,"E375"),sQuery(id+"F0.wireOp",EDGE,"E376"),sQuery(id+"F0.wireOp",EDGE,"E377"),sQuery(id+"F0.wireOp",EDGE,"E378"),sQuery(id+"F0.wireOp",EDGE,"E379"),sQuery(id+"F0.wireOp",EDGE,"E380"),sQuery(id+"F0.wireOp",EDGE,"E381"),sQuery(id+"F0.wireOp",EDGE,"E382"),sQuery(id+"F0.wireOp",EDGE,"E383"),sQuery(id+"F0.wireOp",EDGE,"E384"),sQuery(id+"F0.wireOp",EDGE,"E385"),sQuery(id+"F0.wireOp",EDGE,"E386"),sQuery(id+"F0.wireOp",EDGE,"E387"),sQuery(id+"F0.wireOp",EDGE,"E388"),sQuery(id+"F0.wireOp",EDGE,"E389"),sQuery(id+"F0.wireOp",EDGE,"E390"),sQuery(id+"F0.wireOp",EDGE,"E391"),sQuery(id+"F0.wireOp",EDGE,"E392"),sQuery(id+"F0.wireOp",EDGE,"E393"),sQuery(id+"F0.wireOp",EDGE,"E394"),sQuery(id+"F0.wireOp",EDGE,"E395"),sQuery(id+"F0.wireOp",EDGE,"E396"),sQuery(id+"F0.wireOp",EDGE,"E397"),sQuery(id+"F0.wireOp",EDGE,"E398"),sQuery(id+"F0.wireOp",EDGE,"E399"),sQuery(id+"F0.wireOp",EDGE,"E400"),sQuery(id+"F0.wireOp",EDGE,"E401"),sQuery(id+"F0.wireOp",EDGE,"E402"),sQuery(id+"F0.wireOp",EDGE,"E403"),sQuery(id+"F0.wireOp",EDGE,"E404"),sQuery(id+"F0.wireOp",EDGE,"E405"),sQuery(id+"F0.wireOp",EDGE,"E406"),sQuery(id+"F0.wireOp",EDGE,"E407"),sQuery(id+"F0.wireOp",EDGE,"E408"),sQuery(id+"F0.wireOp",EDGE,"E409"),sQuery(id+"F0.wireOp",EDGE,"E410"),sQuery(id+"F0.wireOp",EDGE,"E411"),sQuery(id+"F0.wireOp",EDGE,"E412"),sQuery(id+"F0.wireOp",EDGE,"E413"),sQuery(id+"F0.wireOp",EDGE,"E414"),sQuery(id+"F0.wireOp",EDGE,"E415"),sQuery(id+"F0.wireOp",EDGE,"E416"),sQuery(id+"F0.wireOp",EDGE,"E417"),sQuery(id+"F0.wireOp",EDGE,"E418"),sQuery(id+"F0.wireOp",EDGE,"E419"),sQuery(id+"F0.wireOp",EDGE,"E420"),sQuery(id+"F0.wireOp",EDGE,"E421"),sQuery(id+"F0.wireOp",EDGE,"E422"),sQuery(id+"F0.wireOp",EDGE,"E423"),sQuery(id+"F0.wireOp",EDGE,"E424"),sQuery(id+"F0.wireOp",EDGE,"E425"),sQuery(id+"F0.wireOp",EDGE,"E426"),sQuery(id+"F0.wireOp",EDGE,"E427"),sQuery(id+"F0.wireOp",EDGE,"E428"),sQuery(id+"F0.wireOp",EDGE,"E429"),sQuery(id+"F0.wireOp",EDGE,"E430"),sQuery(id+"F0.wireOp",EDGE,"E431"),sQuery(id+"F0.wireOp",EDGE,"E432"),sQuery(id+"F0.wireOp",EDGE,"E433"),sQuery(id+"F0.wireOp",EDGE,"E434"),sQuery(id+"F0.wireOp",EDGE,"E435"),sQuery(id+"F0.wireOp",EDGE,"E436"),sQuery(id+"F0.wireOp",EDGE,"E437"),sQuery(id+"F0.wireOp",EDGE,"E438"),sQuery(id+"F0.wireOp",EDGE,"E439"),sQuery(id+"F0.wireOp",EDGE,"E440"),sQuery(id+"F0.wireOp",EDGE,"E441"),sQuery(id+"F0.wireOp",EDGE,"E442"),sQuery(id+"F0.wireOp",EDGE,"E443"),sQuery(id+"F0.wireOp",EDGE,"E444"),sQuery(id+"F0.wireOp",EDGE,"E445"),sQuery(id+"F0.wireOp",EDGE,"E446"),sQuery(id+"F0.wireOp",EDGE,"E447"),sQuery(id+"F0.wireOp",EDGE,"E448"),sQuery(id+"F0.wireOp",EDGE,"E449"),sQuery(id+"F0.wireOp",EDGE,"E450"),sQuery(id+"F0.wireOp",EDGE,"E451"),sQuery(id+"F0.wireOp",EDGE,"E452"),sQuery(id+"F0.wireOp",EDGE,"E453"),sQuery(id+"F0.wireOp",EDGE,"E454"),sQuery(id+"F0.wireOp",EDGE,"E455"),sQuery(id+"F0.wireOp",EDGE,"E456"),sQuery(id+"F0.wireOp",EDGE,"E457"),sQuery(id+"F0.wireOp",EDGE,"E458"),sQuery(id+"F0.wireOp",EDGE,"E459"),sQuery(id+"F0.wireOp",EDGE,"E460"),sQuery(id+"F0.wireOp",EDGE,"E461"),sQuery(id+"F0.wireOp",EDGE,"E462"),sQuery(id+"F0.wireOp",EDGE,"E463"),sQuery(id+"F0.wireOp",EDGE,"E464"),sQuery(id+"F0.wireOp",EDGE,"E465"),sQuery(id+"F0.wireOp",EDGE,"E466"),sQuery(id+"F0.wireOp",EDGE,"E467"),sQuery(id+"F0.wireOp",EDGE,"E468"),sQuery(id+"F0.wireOp",EDGE,"E469"),sQuery(id+"F0.wireOp",EDGE,"E470"),sQuery(id+"F0.wireOp",EDGE,"E471"),sQuery(id+"F0.wireOp",EDGE,"E472"),sQuery(id+"F0.wireOp",EDGE,"E473"),sQuery(id+"F0.wireOp",EDGE,"E474"),sQuery(id+"F0.wireOp",EDGE,"E475"),sQuery(id+"F0.wireOp",EDGE,"E476"),sQuery(id+"F0.wireOp",EDGE,"E477"),sQuery(id+"F0.wireOp",EDGE,"E478"),sQuery(id+"F0.wireOp",EDGE,"E479"),sQuery(id+"F0.wireOp",EDGE,"E480"),sQuery(id+"F0.wireOp",EDGE,"E481"),sQuery(id+"F0.wireOp",EDGE,"E482"),sQuery(id+"F0.wireOp",EDGE,"E483"),sQuery(id+"F0.wireOp",EDGE,"E484"),sQuery(id+"F0.wireOp",EDGE,"E485"),sQuery(id+"F0.wireOp",EDGE,"E486"),sQuery(id+"F0.wireOp",EDGE,"E487"),sQuery(id+"F0.wireOp",EDGE,"E488"),sQuery(id+"F0.wireOp",EDGE,"E489"),sQuery(id+"F0.wireOp",EDGE,"E490"),sQuery(id+"F0.wireOp",EDGE,"E491"),sQuery(id+"F0.wireOp",EDGE,"E492"),sQuery(id+"F0.wireOp",EDGE,"E493"),sQuery(id+"F0.wireOp",EDGE,"E494"),sQuery(id+"F0.wireOp",EDGE,"E495"),sQuery(id+"F0.wireOp",EDGE,"E496"),sQuery(id+"F0.wireOp",EDGE,"E497"),sQuery(id+"F0.wireOp",EDGE,"E498"),sQuery(id+"F0.wireOp",EDGE,"E499"),sQuery(id+"F0.wireOp",EDGE,"E500"),sQuery(id+"F0.wireOp",EDGE,"E501"),sQuery(id+"F0.wireOp",EDGE,"E502"),sQuery(id+"F0.wireOp",EDGE,"E503"),sQuery(id+"F0.wireOp",EDGE,"E504"),sQuery(id+"F0.wireOp",EDGE,"E505"),sQuery(id+"F0.wireOp",EDGE,"E506"),sQuery(id+"F0.wireOp",EDGE,"E507"),sQuery(id+"F0.wireOp",EDGE,"E508"),sQuery(id+"F0.wireOp",EDGE,"E509"),sQuery(id+"F0.wireOp",EDGE,"E510"),sQuery(id+"F0.wireOp",EDGE,"E511"),sQuery(id+"F0.wireOp",EDGE,"E512"),sQuery(id+"F0.wireOp",EDGE,"E513"),sQuery(id+"F0.wireOp",EDGE,"E514"),sQuery(id+"F0.wireOp",EDGE,"E515"),sQuery(id+"F0.wireOp",EDGE,"E516"),sQuery(id+"F0.wireOp",EDGE,"E517"),sQuery(id+"F0.wireOp",EDGE,"E518"),sQuery(id+"F0.wireOp",EDGE,"E519"),sQuery(id+"F0.wireOp",EDGE,"E520"),sQuery(id+"F0.wireOp",EDGE,"E521"),sQuery(id+"F0.wireOp",EDGE,"E522"),sQuery(id+"F0.wireOp",EDGE,"E523"),sQuery(id+"F0.wireOp",EDGE,"E524"),sQuery(id+"F0.wireOp",EDGE,"E525"),sQuery(id+"F0.wireOp",EDGE,"E526"),sQuery(id+"F0.wireOp",EDGE,"E527"),sQuery(id+"F0.wireOp",EDGE,"E528"),sQuery(id+"F0.wireOp",EDGE,"E529"),sQuery(id+"F0.wireOp",EDGE,"E530"),sQuery(id+"F0.wireOp",EDGE,"E531"),sQuery(id+"F0.wireOp",EDGE,"E532"),sQuery(id+"F0.wireOp",EDGE,"E533"),sQuery(id+"F0.wireOp",EDGE,"E534"),sQuery(id+"F0.wireOp",EDGE,"E535"),sQuery(id+"F0.wireOp",EDGE,"E536"),sQuery(id+"F0.wireOp",EDGE,"E537"),sQuery(id+"F0.wireOp",EDGE,"E538"),sQuery(id+"F0.wireOp",EDGE,"E539"),sQuery(id+"F0.wireOp",EDGE,"E540"),sQuery(id+"F0.wireOp",EDGE,"E541"),sQuery(id+"F0.wireOp",EDGE,"E542"),sQuery(id+"F0.wireOp",EDGE,"E543"),sQuery(id+"F0.wireOp",EDGE,"E544"),sQuery(id+"F0.wireOp",EDGE,"E545"),sQuery(id+"F0.wireOp",EDGE,"E546"),sQuery(id+"F0.wireOp",EDGE,"E547"),sQuery(id+"F0.wireOp",EDGE,"E548"),sQuery(id+"F0.wireOp",EDGE,"E549"),sQuery(id+"F0.wireOp",EDGE,"E550"),sQuery(id+"F0.wireOp",EDGE,"E551"),sQuery(id+"F0.wireOp",EDGE,"E552"),sQuery(id+"F0.wireOp",EDGE,"E553"),sQuery(id+"F0.wireOp",EDGE,"E554"),sQuery(id+"F0.wireOp",EDGE,"E555"),sQuery(id+"F0.wireOp",EDGE,"E556"),sQuery(id+"F0.wireOp",EDGE,"E557"),sQuery(id+"F0.wireOp",EDGE,"E558"),sQuery(id+"F0.wireOp",EDGE,"E559"),sQuery(id+"F0.wireOp",EDGE,"E560"),sQuery(id+"F0.wireOp",EDGE,"E561"),sQuery(id+"F0.wireOp",EDGE,"E562"),sQuery(id+"F0.wireOp",EDGE,"E563"),sQuery(id+"F0.wireOp",EDGE,"E564"),sQuery(id+"F0.wireOp",EDGE,"E565"),sQuery(id+"F0.wireOp",EDGE,"E566"),sQuery(id+"F0.wireOp",EDGE,"E567"),sQuery(id+"F0.wireOp",EDGE,"E568"),sQuery(id+"F0.wireOp",EDGE,"E569"),sQuery(id+"F0.wireOp",EDGE,"E571")])],"isStart":false});
            var sketch = newSketch(context, id + "F3", { "sketchPlane" : qUnion([Q0])});
            skCircle(sketch, "E572", {"center": v(-4.59, 0) * mm, "radius": 2.6 * mm});
            skCircle(sketch, "E573", {"center": v(-4.59, 0) * mm, "radius": 4.9 * mm});
            skSolve(sketch);
        }
        {
            var Q0;
            Q0=makeQuery(id+"F3.imprint","IMPRINT",FACE,{"disambiguationData":[TD([[makeQuery(id+"F3.imprint","IMPRINT",EDGE,{"derivedFrom":sQuery(id+"F3.wireOp",EDGE,"E573")}),-1.0]])]});
            extrude(context, id + "F4", {"entities" : qUnion([Q0]), "operationType" : NewBodyOperationType.ADD, "depth" : 1.6 * mm, "offsetDistance" : 25.4 * mm});
        }
        {
            var Q0;
            Q0=makeQuery(id+"F1.opExtrude","CAP_EDGE",EDGE,{"disambiguationData":[OSD([sQuery(id+"F0.wireOp",EDGE,"E571")])],"isStart":false});
            chamfer(context, id + "F5", {"entities" : qUnion([Q0]), "chamferType" : ChamferType.TWO_OFFSETS, "width1" : 2.3 * mm, "oppositeDirection" : false, "width2" : 4 * mm, "tangentPropagation" : true});
        }
        {
            var Q0;
            Q0=makeQuery(id+"F3.imprint","IMPRINT",FACE,{"disambiguationData":[TD([[makeQuery(id+"F3.imprint","IMPRINT",EDGE,{"derivedFrom":sQuery(id+"F3.wireOp",EDGE,"E572")}),1.0]])]});
            extrude(context, id + "F6", {"entities" : qUnion([Q0]), "operationType" : NewBodyOperationType.REMOVE, "oppositeDirection" : true, "depth" : 25.4 * mm, "offsetDistance" : 25.4 * mm});
        }
    });
